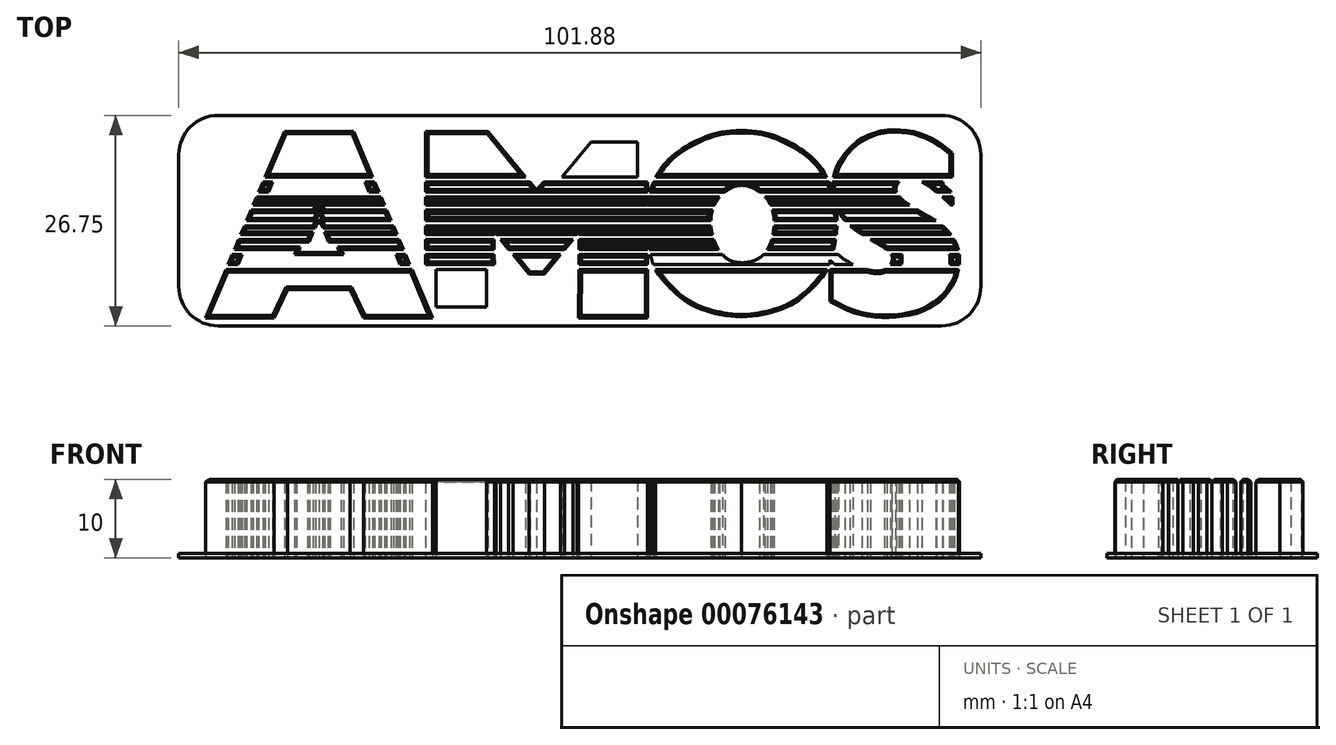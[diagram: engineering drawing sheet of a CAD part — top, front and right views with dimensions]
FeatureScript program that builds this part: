
annotation { "Feature Type Name" : "Feature", "Feature Type Description" : "" }
export const myFeature = defineFeature(function(context is Context, id is Id, definition is map)
    precondition{}
    {
        {
            var Q0;
            Q0=qCreatedBy(makeId("Top.planeOp"),FACE);
            var sketch = newSketch(context, id + "F0", { "sketchPlane" : qUnion([Q0])});
            skLineSegment(sketch, "E0", {"start": v(-45.6, -34.47) * mm, "end": v(-36.87, -34.47) * mm});
            skLineSegment(sketch, "E1", {"start": v(-36.87, -34.47) * mm, "end": v(-35.18, -30.82) * mm});
            skLineSegment(sketch, "E2", {"start": v(-35.18, -30.82) * mm, "end": v(-31.2, -30.82) * mm});
            skLineSegment(sketch, "E3", {"start": v(-45.6, -34.47) * mm, "end": v(-35.6, -10.76) * mm});
            skLineSegment(sketch, "E4", {"start": v(-35.6, -10.76) * mm, "end": v(-31.2, -10.76) * mm});
            skLineSegment(sketch, "E5", {"start": v(-31.2, -10.76) * mm, "end": v(-31.2, -30.82) * mm});
            skLineSegment(sketch, "E6", {"start": v(-43.85, -33.24) * mm, "end": v(-34.99, -12.25) * mm});
            skLineSegment(sketch, "E7", {"start": v(-34.99, -12.25) * mm, "end": v(-31.2, -12.25) * mm});
            skLineSegment(sketch, "E8", {"start": v(-43.85, -33.24) * mm, "end": v(-37.5, -33.24) * mm});
            skLineSegment(sketch, "E9", {"start": v(-37.5, -33.24) * mm, "end": v(-35.93, -29.53) * mm});
            skLineSegment(sketch, "E10", {"start": v(-35.93, -29.53) * mm, "end": v(-31.2, -29.53) * mm});
            skLineSegment(sketch, "E11", {"start": v(-31.2, -26.43) * mm, "end": v(-34.3, -26.43) * mm});
            skLineSegment(sketch, "E12", {"start": v(-34.3, -26.43) * mm, "end": v(-31.2, -19.09) * mm});
            skLineSegment(sketch, "E13", {"start": v(-31.2, -16.54) * mm, "end": v(-36.8, -16.54) * mm});
            skLineSegment(sketch, "E14", {"start": v(-36.8, -16.54) * mm, "end": v(-37.07, -17.19) * mm});
            skLineSegment(sketch, "E15", {"start": v(-37.07, -17.19) * mm, "end": v(-31.2, -17.19) * mm});
            skLineSegment(sketch, "E16", {"start": v(-31.2, -18.44) * mm, "end": v(-37.6, -18.44) * mm});
            skLineSegment(sketch, "E17", {"start": v(-37.6, -18.44) * mm, "end": v(-37.88, -19.09) * mm});
            skLineSegment(sketch, "E18", {"start": v(-37.88, -19.09) * mm, "end": v(-31.2, -19.09) * mm});
            skLineSegment(sketch, "E19", {"start": v(-31.65, -20.13) * mm, "end": v(-38.32, -20.13) * mm});
            skLineSegment(sketch, "E20", {"start": v(-38.32, -20.13) * mm, "end": v(-38.59, -20.78) * mm});
            skLineSegment(sketch, "E21", {"start": v(-38.59, -20.78) * mm, "end": v(-31.92, -20.78) * mm});
            skLineSegment(sketch, "E22", {"start": v(-33.22, -23.86) * mm, "end": v(-39.9, -23.86) * mm});
            skLineSegment(sketch, "E23", {"start": v(-39.9, -23.86) * mm, "end": v(-40.16, -24.5) * mm});
            skLineSegment(sketch, "E24", {"start": v(-40.16, -24.5) * mm, "end": v(-33.5, -24.5) * mm});
            skLineSegment(sketch, "E25", {"start": v(-34.03, -25.78) * mm, "end": v(-40.7, -25.78) * mm});
            skLineSegment(sketch, "E26", {"start": v(-40.7, -25.78) * mm, "end": v(-40.98, -26.43) * mm});
            skLineSegment(sketch, "E27", {"start": v(-40.98, -26.43) * mm, "end": v(-34.3, -26.43) * mm});
            skLineSegment(sketch, "E28", {"start": v(-31.2, -27.66) * mm, "end": v(-41.5, -27.66) * mm});
            skLineSegment(sketch, "E29", {"start": v(-41.5, -27.66) * mm, "end": v(-41.78, -28.33) * mm});
            skLineSegment(sketch, "E30", {"start": v(-41.78, -28.33) * mm, "end": v(-31.2, -28.33) * mm});
            skLineSegment(sketch, "E31", {"start": v(-32.48, -22.11) * mm, "end": v(-39.15, -22.11) * mm});
            skLineSegment(sketch, "E32", {"start": v(-32.76, -22.76) * mm, "end": v(-39.43, -22.76) * mm});
            skLineSegment(sketch, "E33", {"start": v(-31.2, -21.08) * mm, "end": v(-33.1, -25.55) * mm});
            skLineSegment(sketch, "E34", {"start": v(-33.1, -25.55) * mm, "end": v(-31.2, -25.55) * mm});
            skLineSegment(sketch, "E35.MirrorCS", {"start": v(-25.6, -16.54) * mm, "end": v(-25.34, -17.19) * mm});
            skLineSegment(sketch, "E36.MirrorCS", {"start": v(-22.52, -23.86) * mm, "end": v(-22.24, -24.5) * mm});
            skLineSegment(sketch, "E37.MirrorCS", {"start": v(-20.91, -27.66) * mm, "end": v(-20.63, -28.33) * mm});
            skLineSegment(sketch, "E38.MirrorCS", {"start": v(-21.7, -25.78) * mm, "end": v(-21.43, -26.43) * mm});
            skLineSegment(sketch, "E39.MirrorCS", {"start": v(-24.8, -18.44) * mm, "end": v(-24.53, -19.09) * mm});
            skLineSegment(sketch, "E40.MirrorCS", {"start": v(-24.1, -20.13) * mm, "end": v(-23.82, -20.78) * mm});
            skLineSegment(sketch, "E41.MirrorCS", {"start": v(-20.63, -28.33) * mm, "end": v(-31.2, -28.33) * mm});
            skLineSegment(sketch, "E42.MirrorCS", {"start": v(-31.2, -27.66) * mm, "end": v(-20.91, -27.66) * mm});
            skLineSegment(sketch, "E43.MirrorCS", {"start": v(-21.43, -26.43) * mm, "end": v(-28.1, -26.43) * mm});
            skLineSegment(sketch, "E44.MirrorCS", {"start": v(-29.19, -23.86) * mm, "end": v(-22.52, -23.86) * mm});
            skLineSegment(sketch, "E45.MirrorCS", {"start": v(-28.1, -26.43) * mm, "end": v(-31.2, -19.09) * mm});
            skLineSegment(sketch, "E46.MirrorCS", {"start": v(-29.65, -22.76) * mm, "end": v(-22.98, -22.76) * mm});
            skLineSegment(sketch, "E47.MirrorCS", {"start": v(-28.38, -25.78) * mm, "end": v(-21.7, -25.78) * mm});
            skLineSegment(sketch, "E48.MirrorCS", {"start": v(-31.2, -18.44) * mm, "end": v(-24.8, -18.44) * mm});
            skLineSegment(sketch, "E49.MirrorCS", {"start": v(-30.76, -20.13) * mm, "end": v(-24.1, -20.13) * mm});
            skLineSegment(sketch, "E50.MirrorCS", {"start": v(-26.47, -29.53) * mm, "end": v(-31.2, -29.53) * mm});
            skLineSegment(sketch, "E51.MirrorCS", {"start": v(-18.55, -33.24) * mm, "end": v(-24.9, -33.24) * mm});
            skLineSegment(sketch, "E52.MirrorCS", {"start": v(-27.42, -12.25) * mm, "end": v(-31.2, -12.25) * mm});
            skLineSegment(sketch, "E53.MirrorCS", {"start": v(-18.55, -33.24) * mm, "end": v(-27.42, -12.25) * mm});
            skLineSegment(sketch, "E54.MirrorCS", {"start": v(-26.82, -10.76) * mm, "end": v(-31.2, -10.76) * mm});
            skLineSegment(sketch, "E55.MirrorCS", {"start": v(-25.34, -17.19) * mm, "end": v(-31.2, -17.19) * mm});
            skLineSegment(sketch, "E56.MirrorCS", {"start": v(-16.8, -34.47) * mm, "end": v(-26.82, -10.76) * mm});
            skLineSegment(sketch, "E57.MirrorCS", {"start": v(-27.23, -30.82) * mm, "end": v(-31.2, -30.82) * mm});
            skLineSegment(sketch, "E58.MirrorCS", {"start": v(-24.9, -33.24) * mm, "end": v(-26.47, -29.53) * mm});
            skLineSegment(sketch, "E59.MirrorCS", {"start": v(-25.54, -34.47) * mm, "end": v(-27.23, -30.82) * mm});
            skLineSegment(sketch, "E60.MirrorCS", {"start": v(-29.93, -22.11) * mm, "end": v(-23.26, -22.11) * mm});
            skLineSegment(sketch, "E61.MirrorCS", {"start": v(-29.32, -25.55) * mm, "end": v(-31.2, -25.55) * mm});
            skLineSegment(sketch, "E62.MirrorCS", {"start": v(-16.8, -34.47) * mm, "end": v(-25.54, -34.47) * mm});
            skLineSegment(sketch, "E63.MirrorCS", {"start": v(-23.82, -20.78) * mm, "end": v(-30.5, -20.78) * mm});
            skLineSegment(sketch, "E64.MirrorCS", {"start": v(-24.53, -19.09) * mm, "end": v(-31.2, -19.09) * mm});
            skLineSegment(sketch, "E65.MirrorCS", {"start": v(-31.2, -16.54) * mm, "end": v(-25.6, -16.54) * mm});
            skLineSegment(sketch, "E66.MirrorCS", {"start": v(-31.2, -21.08) * mm, "end": v(-29.32, -25.55) * mm});
            skLineSegment(sketch, "E67.MirrorCS", {"start": v(-31.2, -26.43) * mm, "end": v(-28.1, -26.43) * mm});
            skLineSegment(sketch, "E68.MirrorCS", {"start": v(-22.24, -24.5) * mm, "end": v(-28.91, -24.5) * mm});
            skLineSegment(sketch, "E69", {"start": v(-8.88, -34.47) * mm, "end": v(-17.64, -34.47) * mm});
            skLineSegment(sketch, "E70", {"start": v(-17.64, -34.47) * mm, "end": v(-17.64, -10.76) * mm});
            skLineSegment(sketch, "E71", {"start": v(-17.64, -10.76) * mm, "end": v(-9.73, -10.76) * mm});
            skLineSegment(sketch, "E72", {"start": v(-9.73, -10.76) * mm, "end": v(-3.54, -18.24) * mm});
            skLineSegment(sketch, "E73", {"start": v(-3.54, -28.9) * mm, "end": v(-4.5, -28.9) * mm});
            skLineSegment(sketch, "E74", {"start": v(-4.5, -28.9) * mm, "end": v(-8.95, -23.54) * mm});
            skLineSegment(sketch, "E75", {"start": v(-8.95, -23.54) * mm, "end": v(-8.88, -34.47) * mm});
            skLineSegment(sketch, "E76", {"start": v(-3.54, -28.9) * mm, "end": v(-3.54, -18.24) * mm});
            skLineSegment(sketch, "E77", {"start": v(-16.34, -12.09) * mm, "end": v(-10.43, -12.09) * mm});
            skLineSegment(sketch, "E78", {"start": v(-10.43, -12.09) * mm, "end": v(-3.54, -20.42) * mm});
            skLineSegment(sketch, "E79", {"start": v(-16.34, -12.09) * mm, "end": v(-16.34, -33.1) * mm});
            skLineSegment(sketch, "E80", {"start": v(-16.34, -33.1) * mm, "end": v(-9.91, -33.1) * mm});
            skLineSegment(sketch, "E81", {"start": v(-9.91, -33.1) * mm, "end": v(-9.99, -20.8) * mm});
            skLineSegment(sketch, "E82", {"start": v(-9.99, -20.8) * mm, "end": v(-4.44, -27.52) * mm});
            skLineSegment(sketch, "E83", {"start": v(-4.44, -27.52) * mm, "end": v(-3.54, -27.52) * mm});
            skLineSegment(sketch, "E84", {"start": v(-36.8, -16.54) * mm, "end": v(52.85, -16.54) * mm});
            skLineSegment(sketch, "E85", {"start": v(-37.07, -17.19) * mm, "end": v(52.85, -17.19) * mm});
            skLineSegment(sketch, "E86", {"start": v(-37.6, -18.44) * mm, "end": v(52.85, -18.44) * mm});
            skLineSegment(sketch, "E87", {"start": v(-37.88, -19.09) * mm, "end": v(52.85, -19.09) * mm});
            skLineSegment(sketch, "E88", {"start": v(-38.32, -20.13) * mm, "end": v(52.85, -20.13) * mm});
            skLineSegment(sketch, "E89", {"start": v(-38.59, -20.78) * mm, "end": v(52.85, -20.78) * mm});
            skLineSegment(sketch, "E90", {"start": v(-39.15, -22.11) * mm, "end": v(52.85, -22.11) * mm});
            skLineSegment(sketch, "E91", {"start": v(-39.43, -22.76) * mm, "end": v(52.85, -22.76) * mm});
            skLineSegment(sketch, "E92", {"start": v(-39.9, -23.86) * mm, "end": v(52.85, -23.86) * mm});
            skLineSegment(sketch, "E93", {"start": v(-40.16, -24.5) * mm, "end": v(52.85, -24.5) * mm});
            skLineSegment(sketch, "E94", {"start": v(-40.7, -25.78) * mm, "end": v(52.85, -25.78) * mm});
            skLineSegment(sketch, "E95", {"start": v(-40.98, -26.43) * mm, "end": v(52.85, -26.43) * mm});
            skLineSegment(sketch, "E96", {"start": v(-41.5, -27.66) * mm, "end": v(52.85, -27.66) * mm});
            skLineSegment(sketch, "E97", {"start": v(-41.78, -28.33) * mm, "end": v(52.85, -28.33) * mm});
            skLineSegment(sketch, "E98.MirrorCS", {"start": v(-3.54, -28.9) * mm, "end": v(-2.57, -28.9) * mm});
            skLineSegment(sketch, "E99.MirrorCS", {"start": v(-2.65, -27.52) * mm, "end": v(-3.54, -27.52) * mm});
            skLineSegment(sketch, "E100.MirrorCS", {"start": v(1.87, -23.54) * mm, "end": v(1.8, -34.47) * mm});
            skLineSegment(sketch, "E101.MirrorCS", {"start": v(3.35, -12.09) * mm, "end": v(-3.54, -20.42) * mm});
            skLineSegment(sketch, "E102.MirrorCS", {"start": v(-2.57, -28.9) * mm, "end": v(1.87, -23.54) * mm});
            skLineSegment(sketch, "E103.MirrorCS", {"start": v(2.65, -10.76) * mm, "end": v(-3.54, -18.24) * mm});
            skLineSegment(sketch, "E104.MirrorCS", {"start": v(10.56, -10.76) * mm, "end": v(2.65, -10.76) * mm});
            skLineSegment(sketch, "E105.MirrorCS", {"start": v(2.9, -20.8) * mm, "end": v(-2.65, -27.52) * mm});
            skLineSegment(sketch, "E106.MirrorCS", {"start": v(10.56, -34.47) * mm, "end": v(10.56, -10.76) * mm});
            skLineSegment(sketch, "E107.MirrorCS", {"start": v(2.83, -33.1) * mm, "end": v(2.9, -20.8) * mm});
            skLineSegment(sketch, "E108.MirrorCS", {"start": v(1.8, -34.47) * mm, "end": v(10.56, -34.47) * mm});
            skLineSegment(sketch, "E109.MirrorCS", {"start": v(9.26, -33.1) * mm, "end": v(2.83, -33.1) * mm});
            skLineSegment(sketch, "E110.MirrorCS", {"start": v(9.26, -12.09) * mm, "end": v(3.35, -12.09) * mm});
            skLineSegment(sketch, "E111.MirrorCS", {"start": v(9.26, -12.09) * mm, "end": v(9.26, -33.1) * mm});
            skFitSpline(sketch, "E112", {"points": [v(22.46, -10.68) * mm, v(18.17, -11.35) * mm, v(14.47, -13.3) * mm, v(11.9, -16.04) * mm, v(10.3, -21.26) * mm, v(11.13, -27.27) * mm, v(12.26, -29.34) * mm, v(15.78, -32.6) * mm, v(22.46, -34.35) * mm], "startDerivative": vector(-46.81, 1.11) * mm, "endDerivative": vector(48.92, -2.68) * mm});
            skLineSegment(sketch, "E113", {"start": v(22.46, -10.68) * mm, "end": v(22.46, -34.35) * mm});
            skFitSpline(sketch, "E114.0", {"points": [v(22.43, -11.92) * mm, v(21.97, -11.9) * mm, v(21.17, -11.92) * mm, v(20.2, -12.04) * mm, v(19.5, -12.21) * mm, v(18.94, -12.4) * mm, v(18.5, -12.56) * mm, v(18.03, -12.74) * mm, v(17.4, -13.02) * mm, v(16.63, -13.4) * mm, v(15.73, -13.93) * mm, v(14.92, -14.48) * mm, v(14.24, -15.07) * mm, v(13.64, -15.7) * mm, v(13.1, -16.44) * mm, v(12.6, -17.3) * mm, v(12.17, -18.3) * mm, v(11.83, -19.38) * mm, v(11.6, -20.56) * mm, v(11.5, -21.8) * mm, v(11.57, -23.15) * mm, v(11.73, -24.49) * mm, v(11.94, -25.52) * mm, v(12.12, -26.24) * mm, v(12.26, -26.72) * mm, v(12.4, -27.12) * mm, v(12.57, -27.55) * mm, v(12.75, -27.89) * mm, v(12.99, -28.24) * mm, v(13.21, -28.54) * mm, v(13.49, -28.9) * mm, v(13.9, -29.38) * mm, v(14.5, -30.03) * mm, v(15.35, -30.8) * mm, v(16.13, -31.36) * mm, v(16.8, -31.75) * mm, v(17.51, -32.1) * mm, v(18.48, -32.45) * mm, v(20.16, -32.89) * mm, v(21.56, -33.05) * mm, v(22.53, -33.1) * mm]});
            skFitSpline(sketch, "E115.MirrorCS", {"points": [v(22.46, -10.68) * mm, v(26.75, -11.35) * mm, v(30.45, -13.3) * mm, v(33.02, -16.04) * mm, v(34.6, -21.26) * mm, v(33.78, -27.27) * mm, v(32.65, -29.34) * mm, v(29.14, -32.6) * mm, v(22.46, -34.35) * mm], "startDerivative": vector(46.81, 1.11) * mm, "endDerivative": vector(-48.92, -2.68) * mm});
            skFitSpline(sketch, "E116.0", {"points": [v(22.49, -11.97) * mm, v(22.94, -11.96) * mm, v(23.74, -11.98) * mm, v(24.7, -12.1) * mm, v(25.4, -12.26) * mm, v(25.96, -12.44) * mm, v(26.4, -12.6) * mm, v(26.86, -12.8) * mm, v(27.49, -13.06) * mm, v(28.27, -13.45) * mm, v(29.16, -13.97) * mm, v(29.96, -14.53) * mm, v(30.64, -15.1) * mm, v(31.24, -15.74) * mm, v(31.77, -16.47) * mm, v(32.27, -17.33) * mm, v(32.7, -18.3) * mm, v(33.04, -19.4) * mm, v(33.27, -20.56) * mm, v(33.35, -21.8) * mm, v(33.3, -23.15) * mm, v(33.13, -24.48) * mm, v(32.93, -25.5) * mm, v(32.75, -26.23) * mm, v(32.6, -26.7) * mm, v(32.47, -27.1) * mm, v(32.3, -27.53) * mm, v(32.12, -27.86) * mm, v(31.89, -28.21) * mm, v(31.66, -28.51) * mm, v(31.4, -28.86) * mm, v(30.98, -29.35) * mm, v(30.38, -30) * mm, v(29.53, -30.76) * mm, v(28.75, -31.32) * mm, v(28.1, -31.7) * mm, v(27.38, -32.05) * mm, v(26.42, -32.4) * mm, v(24.75, -32.84) * mm, v(23.35, -33) * mm, v(22.39, -33.06) * mm]});
            skFitSpline(sketch, "E117", {"points": [v(49.24, -13.5) * mm, v(46.32, -11.49) * mm, v(42.17, -10.55) * mm, v(38.34, -11.36) * mm, v(35.36, -13.9) * mm, v(34.1, -16.89) * mm, v(34.19, -19.42) * mm, v(34.98, -21.26) * mm, v(36.8, -23.19) * mm, v(40.2, -25.3) * mm, v(41.55, -26.49) * mm, v(41.5, -27.5) * mm, v(40.5, -28.4) * mm, v(38.54, -28.35) * mm, v(35.81, -27.2) * mm, v(33.68, -25.44) * mm], "startDerivative": vector(-34.4, 29.23) * mm, "endDerivative": vector(-30.32, 27.7) * mm});
            skFitSpline(sketch, "E118", {"points": [v(33.68, -32.37) * mm, v(37.2, -33.94) * mm, v(41.36, -34.37) * mm, v(45.32, -33.65) * mm, v(48.33, -31.65) * mm, v(49.9, -28.93) * mm, v(50.1, -26.19) * mm, v(49.33, -24.24) * mm, v(47.6, -22.42) * mm, v(44.8, -20.76) * mm, v(42.36, -18.85) * mm, v(42.12, -17.85) * mm, v(42.74, -17) * mm, v(44.32, -16.74) * mm, v(47.14, -18.37) * mm, v(49.34, -20.42) * mm], "startDerivative": vector(43.54, -22.9) * mm, "endDerivative": vector(27.49, -30.17) * mm});
            skLineSegment(sketch, "E119", {"start": v(33.68, -25.44) * mm, "end": v(33.68, -32.37) * mm});
            skLineSegment(sketch, "E120", {"start": v(49.24, -13.5) * mm, "end": v(49.34, -20.42) * mm});
            skFitSpline(sketch, "E121.0", {"points": [v(48.45, -14.43) * mm, v(48.1, -14.13) * mm, v(47.4, -13.56) * mm, v(46.51, -12.95) * mm, v(45.75, -12.56) * mm, v(45.12, -12.3) * mm, v(44.45, -12.1) * mm, v(43.51, -11.88) * mm, v(42.3, -11.75) * mm, v(40.95, -11.8) * mm, v(39.69, -12.09) * mm, v(38.53, -12.6) * mm, v(37.44, -13.38) * mm, v(36.52, -14.33) * mm, v(35.84, -15.36) * mm, v(35.48, -16.26) * mm, v(35.31, -16.97) * mm, v(35.22, -17.66) * mm, v(35.24, -18.35) * mm, v(35.34, -18.98) * mm, v(35.49, -19.57) * mm, v(35.7, -20.08) * mm, v(36, -20.59) * mm, v(36.35, -21.1) * mm, v(36.8, -21.6) * mm, v(37.32, -22.04) * mm, v(37.66, -22.3) * mm, v(38.03, -22.56) * mm, v(38.55, -22.9) * mm, v(39.23, -23.3) * mm, v(39.9, -23.7) * mm, v(40.57, -24.08) * mm, v(41.18, -24.45) * mm, v(41.65, -24.78) * mm, v(42.01, -25.09) * mm, v(42.26, -25.35) * mm, v(42.46, -25.6) * mm, v(42.6, -25.84) * mm, v(42.72, -26.1) * mm, v(42.83, -26.44) * mm, v(42.89, -27) * mm, v(42.79, -27.65) * mm, v(42.46, -28.34) * mm, v(42.07, -28.82) * mm, v(41.68, -29.15) * mm, v(41.35, -29.36) * mm, v(40.98, -29.54) * mm, v(40.46, -29.7) * mm, v(39.82, -29.77) * mm, v(39.09, -29.72) * mm, v(38.5, -29.6) * mm, v(38.04, -29.5) * mm, v(37.58, -29.36) * mm, v(36.99, -29.16) * mm, v(36.28, -28.86) * mm, v(35.6, -28.52) * mm, v(34.94, -28.1) * mm, v(34.35, -27.67) * mm, v(33.63, -27.07) * mm, v(33.16, -26.62) * mm, v(32.86, -26.34) * mm]});
            skLineSegment(sketch, "E121.1", {"start": v(48.02, -14.07) * mm, "end": v(48.07, -17.55) * mm});
            skFitSpline(sketch, "E121.2", {"points": [v(34.25, -31.28) * mm, v(34.71, -31.52) * mm, v(35.6, -32) * mm, v(36.65, -32.47) * mm, v(37.5, -32.76) * mm, v(38.15, -32.92) * mm, v(38.84, -33.04) * mm, v(39.56, -33.12) * mm, v(40.3, -33.16) * mm, v(41.05, -33.16) * mm, v(41.8, -33.13) * mm, v(42.78, -33.04) * mm, v(43.7, -32.88) * mm, v(44.56, -32.64) * mm, v(45.37, -32.33) * mm, v(46.31, -31.8) * mm, v(47.29, -31.02) * mm, v(48.04, -30.11) * mm, v(48.5, -29.28) * mm, v(48.74, -28.6) * mm, v(48.9, -27.88) * mm, v(48.97, -27.16) * mm, v(48.92, -26.5) * mm, v(48.84, -26.08) * mm, v(48.72, -25.69) * mm, v(48.55, -25.31) * mm, v(48.33, -24.93) * mm, v(48.04, -24.54) * mm, v(47.72, -24.15) * mm, v(47.34, -23.78) * mm, v(47, -23.5) * mm, v(46.7, -23.29) * mm, v(46.23, -22.97) * mm, v(45.57, -22.6) * mm, v(44.71, -22.13) * mm, v(44.03, -21.73) * mm, v(43.33, -21.3) * mm, v(42.66, -20.83) * mm, v(42.04, -20.32) * mm, v(41.5, -19.78) * mm, v(41.13, -19.23) * mm, v(40.94, -18.72) * mm, v(40.86, -18.31) * mm, v(40.86, -17.9) * mm, v(40.93, -17.52) * mm, v(41.05, -17.16) * mm, v(41.28, -16.72) * mm, v(41.68, -16.24) * mm, v(42.3, -15.8) * mm, v(43.04, -15.52) * mm, v(43.71, -15.44) * mm, v(44.27, -15.48) * mm, v(44.7, -15.57) * mm, v(45.1, -15.7) * mm, v(45.62, -15.9) * mm, v(46.24, -16.22) * mm, v(46.93, -16.67) * mm, v(47.59, -17.16) * mm, v(48.2, -17.64) * mm, v(48.75, -18.12) * mm, v(49.46, -18.77) * mm, v(49.94, -19.26) * mm, v(50.24, -19.6) * mm]});
            skLineSegment(sketch, "E121.3", {"start": v(34.9, -28.08) * mm, "end": v(34.9, -31.62) * mm});
            skLineSegment(sketch, "E122", {"start": v(-36.8, -16.54) * mm, "end": v(-52.11, -16.54) * mm});
            skLineSegment(sketch, "E123", {"start": v(-37.07, -17.19) * mm, "end": v(-52.11, -17.19) * mm});
            skLineSegment(sketch, "E124", {"start": v(-37.6, -18.44) * mm, "end": v(-52.11, -18.44) * mm});
            skLineSegment(sketch, "E125", {"start": v(-37.88, -19.09) * mm, "end": v(-52.11, -19.09) * mm});
            skLineSegment(sketch, "E126", {"start": v(-38.32, -20.13) * mm, "end": v(-52.11, -20.13) * mm});
            skLineSegment(sketch, "E127", {"start": v(-38.59, -20.78) * mm, "end": v(-52.11, -20.78) * mm});
            skLineSegment(sketch, "E128", {"start": v(-39.15, -22.11) * mm, "end": v(-52.11, -22.11) * mm});
            skLineSegment(sketch, "E129", {"start": v(-39.43, -22.76) * mm, "end": v(-52.11, -22.76) * mm});
            skLineSegment(sketch, "E130", {"start": v(-39.9, -23.86) * mm, "end": v(-52.11, -23.86) * mm});
            skLineSegment(sketch, "E131", {"start": v(-40.16, -24.5) * mm, "end": v(-52.11, -24.5) * mm});
            skLineSegment(sketch, "E132", {"start": v(-40.7, -25.78) * mm, "end": v(-52.11, -25.78) * mm});
            skLineSegment(sketch, "E133", {"start": v(-40.98, -26.43) * mm, "end": v(-52.11, -26.43) * mm});
            skLineSegment(sketch, "E134", {"start": v(-41.5, -27.66) * mm, "end": v(-52.11, -27.66) * mm});
            skLineSegment(sketch, "E135", {"start": v(-41.78, -28.33) * mm, "end": v(-52.11, -28.33) * mm});
            skFitSpline(sketch, "E136", {"points": [v(22.46, -17.61) * mm, v(19.7, -19.09) * mm, v(18.57, -22.4) * mm, v(20.05, -26.43) * mm, v(22.46, -27.46) * mm, v(25.25, -26.43) * mm, v(26.62, -22.4) * mm, v(25.48, -19.09) * mm, v(22.46, -17.61) * mm]});
            skLineSegment(sketch, "E137.bottom", {"start": v(-47.15, -8.85) * mm, "end": v(52.85, -8.85) * mm});
            skLineSegment(sketch, "E137.top", {"start": v(-47.15, -35.44) * mm, "end": v(52.85, -35.44) * mm});
            skLineSegment(sketch, "E137.left", {"start": v(-47.15, -8.85) * mm, "end": v(-47.15, -35.44) * mm});
            skLineSegment(sketch, "E137.right", {"start": v(52.85, -8.85) * mm, "end": v(52.85, -35.44) * mm, "construction": true});
            skSolve(sketch);
        }
        {
            var Q0;
            {var subQ5=sQuery(id+"F0.wireOp",EDGE,"E4");Q0=makeQuery(id+"F0.imprint","IMPRINT",FACE,{"disambiguationData":[TD([[makeQuery(id+"F0.imprint","IMPRINT",EDGE,{"derivedFrom":subQ5}),-1.0]])]});}
            extrude(context, id + "F1", {"entities" : qUnion([Q0]), "depth" : 10 * mm});
        }
        {
            var Q0;
            {var subQ2=sQuery(id+"F0.wireOp",EDGE,"E52.MirrorCS");Q0=makeQuery(id+"F0.imprint","IMPRINT",FACE,{"disambiguationData":[TD([[makeQuery(id+"F0.imprint","IMPRINT",EDGE,{"derivedFrom":subQ2}),-1.0]])]});}
            var Q1;
            {var subQ0=sQuery(id+"F0.wireOp",EDGE,"E52.MirrorCS");Q1=makeQuery(id+"F0.imprint","IMPRINT",FACE,{"disambiguationData":[TD([[makeQuery(id+"F0.imprint","IMPRINT",EDGE,{"derivedFrom":subQ0}),1.0]])]});}
            var Q2;
            {var subQ0=sQuery(id+"F0.wireOp",EDGE,"E7");Q2=makeQuery(id+"F0.imprint","IMPRINT",FACE,{"disambiguationData":[TD([[makeQuery(id+"F0.imprint","IMPRINT",EDGE,{"derivedFrom":subQ0}),-1.0]])]});}
            var Q3;
            {var subQ0=sQuery(id+"F0.wireOp",EDGE,"E86");var subQ1=sQuery(id+"F0.wireOp",EDGE,"E53.MirrorCS");var subQ2=makeQuery(id+"F0.imprint","INTERSECT",VERTEX,{"derivedFrom":[subQ1,subQ0]});Q3=makeQuery(id+"F0.imprint","IMPRINT",FACE,{"disambiguationData":[TD([[makeQuery(id+"F0.imprint","IMPRINT",EDGE,{"disambiguationData":[TD([[subQ2,-1.0]])],"derivedFrom":subQ1}),-1.0]])]});}
            var Q4;
            {var subQ0=sQuery(id+"F0.wireOp",EDGE,"E88");var subQ1=sQuery(id+"F0.wireOp",EDGE,"E53.MirrorCS");var subQ2=makeQuery(id+"F0.imprint","INTERSECT",VERTEX,{"derivedFrom":[subQ1,subQ0]});Q4=makeQuery(id+"F0.imprint","IMPRINT",FACE,{"disambiguationData":[TD([[makeQuery(id+"F0.imprint","IMPRINT",EDGE,{"disambiguationData":[TD([[subQ2,-1.0]])],"derivedFrom":subQ1}),-1.0]])]});}
            var Q5;
            {var subQ0=sQuery(id+"F0.wireOp",EDGE,"E90");var subQ1=sQuery(id+"F0.wireOp",EDGE,"E53.MirrorCS");var subQ2=makeQuery(id+"F0.imprint","INTERSECT",VERTEX,{"derivedFrom":[subQ1,subQ0]});Q5=makeQuery(id+"F0.imprint","IMPRINT",FACE,{"disambiguationData":[TD([[makeQuery(id+"F0.imprint","IMPRINT",EDGE,{"disambiguationData":[TD([[subQ2,-1.0]])],"derivedFrom":subQ1}),-1.0]])]});}
            var Q6;
            {var subQ0=sQuery(id+"F0.wireOp",EDGE,"E92");var subQ1=sQuery(id+"F0.wireOp",EDGE,"E53.MirrorCS");var subQ2=makeQuery(id+"F0.imprint","INTERSECT",VERTEX,{"derivedFrom":[subQ1,subQ0]});Q6=makeQuery(id+"F0.imprint","IMPRINT",FACE,{"disambiguationData":[TD([[makeQuery(id+"F0.imprint","IMPRINT",EDGE,{"disambiguationData":[TD([[subQ2,-1.0]])],"derivedFrom":subQ1}),-1.0]])]});}
            var Q7;
            {var subQ0=sQuery(id+"F0.wireOp",EDGE,"E94");var subQ1=sQuery(id+"F0.wireOp",EDGE,"E53.MirrorCS");var subQ2=makeQuery(id+"F0.imprint","INTERSECT",VERTEX,{"derivedFrom":[subQ1,subQ0]});Q7=makeQuery(id+"F0.imprint","IMPRINT",FACE,{"disambiguationData":[TD([[makeQuery(id+"F0.imprint","IMPRINT",EDGE,{"disambiguationData":[TD([[subQ2,-1.0]])],"derivedFrom":subQ1}),-1.0]])]});}
            var Q8;
            {var subQ0=sQuery(id+"F0.wireOp",EDGE,"E96");var subQ1=sQuery(id+"F0.wireOp",EDGE,"E53.MirrorCS");var subQ2=makeQuery(id+"F0.imprint","INTERSECT",VERTEX,{"derivedFrom":[subQ1,subQ0]});Q8=makeQuery(id+"F0.imprint","IMPRINT",FACE,{"disambiguationData":[TD([[makeQuery(id+"F0.imprint","IMPRINT",EDGE,{"disambiguationData":[TD([[subQ2,-1.0]])],"derivedFrom":subQ1}),-1.0]])]});}
            var Q9;
            {var subQ11=sQuery(id+"F0.wireOp",EDGE,"E50.MirrorCS");Q9=makeQuery(id+"F0.imprint","IMPRINT",FACE,{"disambiguationData":[TD([[makeQuery(id+"F0.imprint","IMPRINT",EDGE,{"derivedFrom":subQ11}),1.0]])]});}
            var Q10;
            {var subQ0=sQuery(id+"F0.wireOp",EDGE,"E69");var subQ1=sQuery(id+"F0.wireOp",EDGE,"E56.MirrorCS");var subQ2=makeQuery(id+"F0.imprint","INTERSECT",VERTEX,{"derivedFrom":[subQ1,subQ0]});Q10=makeQuery(id+"F0.imprint","IMPRINT",FACE,{"disambiguationData":[TD([[makeQuery(id+"F0.imprint","IMPRINT",EDGE,{"disambiguationData":[TD([[subQ2,-1.0]])],"derivedFrom":subQ1}),1.0]])]});}
            var Q11;
            {var subQ1=sQuery(id+"F0.wireOp",EDGE,"E0");Q11=makeQuery(id+"F0.imprint","IMPRINT",FACE,{"disambiguationData":[TD([[makeQuery(id+"F0.imprint","IMPRINT",EDGE,{"derivedFrom":subQ1}),1.0]])]});}
            var Q12;
            {var subQ0=sQuery(id+"F0.wireOp",EDGE,"E134");var subQ1=sQuery(id+"F0.wireOp",EDGE,"E3");var subQ2=makeQuery(id+"F0.imprint","INTERSECT",VERTEX,{"derivedFrom":[subQ1,subQ0]});Q12=makeQuery(id+"F0.imprint","IMPRINT",FACE,{"disambiguationData":[TD([[makeQuery(id+"F0.imprint","IMPRINT",EDGE,{"disambiguationData":[TD([[subQ2,-1.0]])],"derivedFrom":subQ1}),-1.0]])]});}
            var Q13;
            {var subQ0=sQuery(id+"F0.wireOp",EDGE,"E132");var subQ1=sQuery(id+"F0.wireOp",EDGE,"E3");var subQ2=makeQuery(id+"F0.imprint","INTERSECT",VERTEX,{"derivedFrom":[subQ1,subQ0]});Q13=makeQuery(id+"F0.imprint","IMPRINT",FACE,{"disambiguationData":[TD([[makeQuery(id+"F0.imprint","IMPRINT",EDGE,{"disambiguationData":[TD([[subQ2,-1.0]])],"derivedFrom":subQ1}),-1.0]])]});}
            var Q14;
            {var subQ0=sQuery(id+"F0.wireOp",EDGE,"E130");var subQ1=sQuery(id+"F0.wireOp",EDGE,"E3");var subQ2=makeQuery(id+"F0.imprint","INTERSECT",VERTEX,{"derivedFrom":[subQ1,subQ0]});Q14=makeQuery(id+"F0.imprint","IMPRINT",FACE,{"disambiguationData":[TD([[makeQuery(id+"F0.imprint","IMPRINT",EDGE,{"disambiguationData":[TD([[subQ2,-1.0]])],"derivedFrom":subQ1}),-1.0]])]});}
            var Q15;
            {var subQ0=sQuery(id+"F0.wireOp",EDGE,"E128");var subQ1=sQuery(id+"F0.wireOp",EDGE,"E3");var subQ2=makeQuery(id+"F0.imprint","INTERSECT",VERTEX,{"derivedFrom":[subQ1,subQ0]});Q15=makeQuery(id+"F0.imprint","IMPRINT",FACE,{"disambiguationData":[TD([[makeQuery(id+"F0.imprint","IMPRINT",EDGE,{"disambiguationData":[TD([[subQ2,-1.0]])],"derivedFrom":subQ1}),-1.0]])]});}
            var Q16;
            {var subQ0=sQuery(id+"F0.wireOp",EDGE,"E126");var subQ1=sQuery(id+"F0.wireOp",EDGE,"E3");var subQ2=makeQuery(id+"F0.imprint","INTERSECT",VERTEX,{"derivedFrom":[subQ1,subQ0]});Q16=makeQuery(id+"F0.imprint","IMPRINT",FACE,{"disambiguationData":[TD([[makeQuery(id+"F0.imprint","IMPRINT",EDGE,{"disambiguationData":[TD([[subQ2,-1.0]])],"derivedFrom":subQ1}),-1.0]])]});}
            var Q17;
            {var subQ0=sQuery(id+"F0.wireOp",EDGE,"E124");var subQ1=sQuery(id+"F0.wireOp",EDGE,"E3");var subQ2=makeQuery(id+"F0.imprint","INTERSECT",VERTEX,{"derivedFrom":[subQ1,subQ0]});Q17=makeQuery(id+"F0.imprint","IMPRINT",FACE,{"disambiguationData":[TD([[makeQuery(id+"F0.imprint","IMPRINT",EDGE,{"disambiguationData":[TD([[subQ2,-1.0]])],"derivedFrom":subQ1}),-1.0]])]});}
            var Q18;
            {var subQ0=sQuery(id+"F0.wireOp",EDGE,"E92");var subQ1=sQuery(id+"F0.wireOp",EDGE,"E12");var subQ2=makeQuery(id+"F0.imprint","INTERSECT",VERTEX,{"derivedFrom":[subQ1,subQ0]});Q18=makeQuery(id+"F0.imprint","IMPRINT",FACE,{"disambiguationData":[TD([[makeQuery(id+"F0.imprint","IMPRINT",EDGE,{"disambiguationData":[TD([[subQ2,-1.0]])],"derivedFrom":subQ1}),-1.0]])]});}
            var Q19;
            {var subQ5=sQuery(id+"F0.wireOp",EDGE,"E34");Q19=makeQuery(id+"F0.imprint","IMPRINT",FACE,{"disambiguationData":[TD([[makeQuery(id+"F0.imprint","IMPRINT",EDGE,{"derivedFrom":subQ5}),-1.0]])]});}
            var Q20;
            {var subQ1=sQuery(id+"F0.wireOp",EDGE,"E61.MirrorCS");Q20=makeQuery(id+"F0.imprint","IMPRINT",FACE,{"disambiguationData":[TD([[makeQuery(id+"F0.imprint","IMPRINT",EDGE,{"derivedFrom":subQ1}),1.0]])]});}
            var Q21;
            {var subQ0=sQuery(id+"F0.wireOp",EDGE,"E92");var subQ1=sQuery(id+"F0.wireOp",EDGE,"E45.MirrorCS");var subQ2=makeQuery(id+"F0.imprint","INTERSECT",VERTEX,{"derivedFrom":[subQ1,subQ0]});Q21=makeQuery(id+"F0.imprint","IMPRINT",FACE,{"disambiguationData":[TD([[makeQuery(id+"F0.imprint","IMPRINT",EDGE,{"disambiguationData":[TD([[subQ2,-1.0]])],"derivedFrom":subQ1}),1.0]])]});}
            var Q22;
            {var subQ3=sQuery(id+"F0.wireOp",EDGE,"E90");var subQ7=sQuery(id+"F0.wireOp",EDGE,"E45.MirrorCS");var subQ9=makeQuery(id+"F0.imprint","INTERSECT",VERTEX,{"derivedFrom":[subQ7,subQ3]});Q22=makeQuery(id+"F0.imprint","IMPRINT",FACE,{"disambiguationData":[TD([[makeQuery(id+"F0.imprint","IMPRINT",EDGE,{"disambiguationData":[TD([[subQ9,-1.0]])],"derivedFrom":subQ7}),1.0]])]});}
            var Q23;
            {var subQ3=sQuery(id+"F0.wireOp",EDGE,"E90");var subQ7=sQuery(id+"F0.wireOp",EDGE,"E12");var subQ9=makeQuery(id+"F0.imprint","INTERSECT",VERTEX,{"derivedFrom":[subQ7,subQ3]});Q23=makeQuery(id+"F0.imprint","IMPRINT",FACE,{"disambiguationData":[TD([[makeQuery(id+"F0.imprint","IMPRINT",EDGE,{"disambiguationData":[TD([[subQ9,-1.0]])],"derivedFrom":subQ7}),-1.0]])]});}
            var Q24;
            {var subQ1=sQuery(id+"F0.wireOp",EDGE,"E5");var subQ3=sQuery(id+"F0.wireOp",EDGE,"E88");var subQ4=makeQuery(id+"F0.imprint","INTERSECT",VERTEX,{"derivedFrom":[subQ1,subQ3]});Q24=makeQuery(id+"F0.imprint","IMPRINT",FACE,{"disambiguationData":[TD([[makeQuery(id+"F0.imprint","IMPRINT",EDGE,{"disambiguationData":[TD([[subQ4,-1.0]])],"derivedFrom":subQ3}),1.0]])]});}
            var Q25;
            {var subQ1=sQuery(id+"F0.wireOp",EDGE,"E5");var subQ3=sQuery(id+"F0.wireOp",EDGE,"E88");var subQ4=makeQuery(id+"F0.imprint","INTERSECT",VERTEX,{"derivedFrom":[subQ1,subQ3]});Q25=makeQuery(id+"F0.imprint","IMPRINT",FACE,{"disambiguationData":[TD([[makeQuery(id+"F0.imprint","IMPRINT",EDGE,{"disambiguationData":[TD([[subQ4,1.0]])],"derivedFrom":subQ3}),1.0]])]});}
            var Q26;
            {var subQ0=sQuery(id+"F0.wireOp",EDGE,"E50.MirrorCS");Q26=makeQuery(id+"F0.imprint","IMPRINT",FACE,{"disambiguationData":[TD([[makeQuery(id+"F0.imprint","IMPRINT",EDGE,{"derivedFrom":subQ0}),-1.0]])]});}
            var Q27;
            {var subQ0=sQuery(id+"F0.wireOp",EDGE,"E8");Q27=makeQuery(id+"F0.imprint","IMPRINT",FACE,{"disambiguationData":[TD([[makeQuery(id+"F0.imprint","IMPRINT",EDGE,{"derivedFrom":subQ0}),1.0]])]});}
            var Q28;
            {var subQ0=sQuery(id+"F0.wireOp",EDGE,"E95");var subQ4=sQuery(id+"F0.wireOp",EDGE,"E5");var subQ5=makeQuery(id+"F0.imprint","INTERSECT",VERTEX,{"derivedFrom":[subQ4,subQ0]});Q28=makeQuery(id+"F0.imprint","IMPRINT",FACE,{"disambiguationData":[TD([[makeQuery(id+"F0.imprint","IMPRINT",EDGE,{"disambiguationData":[TD([[subQ5,-1.0]])],"derivedFrom":subQ4}),1.0]])]});}
            var Q29;
            {var subQ0=sQuery(id+"F0.wireOp",EDGE,"E95");var subQ2=sQuery(id+"F0.wireOp",EDGE,"E5");var subQ3=makeQuery(id+"F0.imprint","INTERSECT",VERTEX,{"derivedFrom":[subQ2,subQ0]});Q29=makeQuery(id+"F0.imprint","IMPRINT",FACE,{"disambiguationData":[TD([[makeQuery(id+"F0.imprint","IMPRINT",EDGE,{"disambiguationData":[TD([[subQ3,-1.0]])],"derivedFrom":subQ2}),-1.0]])]});}
            var Q30;
            {var subQ3=sQuery(id+"F0.wireOp",EDGE,"E94");var subQ5=sQuery(id+"F0.wireOp",EDGE,"E12");var subQ6=makeQuery(id+"F0.imprint","INTERSECT",VERTEX,{"derivedFrom":[subQ5,subQ3]});Q30=makeQuery(id+"F0.imprint","IMPRINT",FACE,{"disambiguationData":[TD([[makeQuery(id+"F0.imprint","IMPRINT",EDGE,{"disambiguationData":[TD([[subQ6,-1.0]])],"derivedFrom":subQ5}),1.0]])]});}
            var Q31;
            {var subQ0=sQuery(id+"F0.wireOp",EDGE,"E94");var subQ1=sQuery(id+"F0.wireOp",EDGE,"E45.MirrorCS");var subQ2=makeQuery(id+"F0.imprint","INTERSECT",VERTEX,{"derivedFrom":[subQ1,subQ0]});Q31=makeQuery(id+"F0.imprint","IMPRINT",FACE,{"disambiguationData":[TD([[makeQuery(id+"F0.imprint","IMPRINT",EDGE,{"disambiguationData":[TD([[subQ2,-1.0]])],"derivedFrom":subQ1}),-1.0]])]});}
            var Q32;
            {var subQ0=sQuery(id+"F0.wireOp",EDGE,"E92");var subQ1=sQuery(id+"F0.wireOp",EDGE,"E45.MirrorCS");var subQ2=makeQuery(id+"F0.imprint","INTERSECT",VERTEX,{"derivedFrom":[subQ1,subQ0]});Q32=makeQuery(id+"F0.imprint","IMPRINT",FACE,{"disambiguationData":[TD([[makeQuery(id+"F0.imprint","IMPRINT",EDGE,{"disambiguationData":[TD([[subQ2,-1.0]])],"derivedFrom":subQ1}),-1.0]])]});}
            var Q33;
            {var subQ0=sQuery(id+"F0.wireOp",EDGE,"E92");var subQ5=sQuery(id+"F0.wireOp",EDGE,"E12");var subQ6=makeQuery(id+"F0.imprint","INTERSECT",VERTEX,{"derivedFrom":[subQ5,subQ0]});Q33=makeQuery(id+"F0.imprint","IMPRINT",FACE,{"disambiguationData":[TD([[makeQuery(id+"F0.imprint","IMPRINT",EDGE,{"disambiguationData":[TD([[subQ6,-1.0]])],"derivedFrom":subQ5}),1.0]])]});}
            var Q34;
            {var subQ3=sQuery(id+"F0.wireOp",EDGE,"E90");var subQ5=sQuery(id+"F0.wireOp",EDGE,"E12");var subQ7=makeQuery(id+"F0.imprint","INTERSECT",VERTEX,{"derivedFrom":[subQ5,subQ3]});Q34=makeQuery(id+"F0.imprint","IMPRINT",FACE,{"disambiguationData":[TD([[makeQuery(id+"F0.imprint","IMPRINT",EDGE,{"disambiguationData":[TD([[subQ7,-1.0]])],"derivedFrom":subQ5}),1.0]])]});}
            var Q35;
            {var subQ0=sQuery(id+"F0.wireOp",EDGE,"E90");var subQ1=sQuery(id+"F0.wireOp",EDGE,"E45.MirrorCS");var subQ2=makeQuery(id+"F0.imprint","INTERSECT",VERTEX,{"derivedFrom":[subQ1,subQ0]});Q35=makeQuery(id+"F0.imprint","IMPRINT",FACE,{"disambiguationData":[TD([[makeQuery(id+"F0.imprint","IMPRINT",EDGE,{"disambiguationData":[TD([[subQ2,-1.0]])],"derivedFrom":subQ1}),-1.0]])]});}
            var Q36;
            {var subQ3=sQuery(id+"F0.wireOp",EDGE,"E88");var subQ5=sQuery(id+"F0.wireOp",EDGE,"E53.MirrorCS");var subQ6=makeQuery(id+"F0.imprint","INTERSECT",VERTEX,{"derivedFrom":[subQ5,subQ3]});Q36=makeQuery(id+"F0.imprint","IMPRINT",FACE,{"disambiguationData":[TD([[makeQuery(id+"F0.imprint","IMPRINT",EDGE,{"disambiguationData":[TD([[subQ6,-1.0]])],"derivedFrom":subQ5}),1.0]])]});}
            var Q37;
            {var subQ3=sQuery(id+"F0.wireOp",EDGE,"E88");var subQ5=sQuery(id+"F0.wireOp",EDGE,"E12");var subQ7=makeQuery(id+"F0.imprint","INTERSECT",VERTEX,{"derivedFrom":[subQ5,subQ3]});Q37=makeQuery(id+"F0.imprint","IMPRINT",FACE,{"disambiguationData":[TD([[makeQuery(id+"F0.imprint","IMPRINT",EDGE,{"disambiguationData":[TD([[subQ7,-1.0]])],"derivedFrom":subQ5}),1.0]])]});}
            var Q38;
            {var subQ0=sQuery(id+"F0.wireOp",EDGE,"E85");var subQ1=sQuery(id+"F0.wireOp",EDGE,"E5");var subQ2=makeQuery(id+"F0.imprint","INTERSECT",VERTEX,{"derivedFrom":[subQ1,subQ0]});Q38=makeQuery(id+"F0.imprint","IMPRINT",FACE,{"disambiguationData":[TD([[makeQuery(id+"F0.imprint","IMPRINT",EDGE,{"disambiguationData":[TD([[subQ2,-1.0]])],"derivedFrom":subQ1}),-1.0]])]});}
            var Q39;
            {var subQ0=sQuery(id+"F0.wireOp",EDGE,"E85");var subQ1=sQuery(id+"F0.wireOp",EDGE,"E5");var subQ2=makeQuery(id+"F0.imprint","INTERSECT",VERTEX,{"derivedFrom":[subQ1,subQ0]});Q39=makeQuery(id+"F0.imprint","IMPRINT",FACE,{"disambiguationData":[TD([[makeQuery(id+"F0.imprint","IMPRINT",EDGE,{"disambiguationData":[TD([[subQ2,-1.0]])],"derivedFrom":subQ1}),1.0]])]});}
            extrude(context, id + "F2", {"entities" : qUnion([Q0, Q1, Q2, Q3, Q4, Q5, Q6, Q7, Q8, Q9, Q10, Q11, Q12, Q13, Q14, Q15, Q16, Q17, Q18, Q19, Q20, Q21, Q22, Q23, Q24, Q25, Q26, Q27, Q28, Q29, Q30, Q31, Q32, Q33, Q34, Q35, Q36, Q37, Q38, Q39]), "operationType" : NewBodyOperationType.ADD, "depth" : 10 * mm});
        }
        {
            var Q0;
            {var subQ5=sQuery(id+"F0.wireOp",EDGE,"E71");Q0=makeQuery(id+"F0.imprint","IMPRINT",FACE,{"disambiguationData":[TD([[makeQuery(id+"F0.imprint","IMPRINT",EDGE,{"derivedFrom":subQ5}),-1.0]])]});}
            var Q1;
            {var subQ0=sQuery(id+"F0.wireOp",EDGE,"E104.MirrorCS");Q1=makeQuery(id+"F0.imprint","IMPRINT",FACE,{"disambiguationData":[TD([[makeQuery(id+"F0.imprint","IMPRINT",EDGE,{"derivedFrom":subQ0}),1.0]])]});}
            var Q2;
            {var subQ5=sQuery(id+"F0.wireOp",EDGE,"E110.MirrorCS");Q2=makeQuery(id+"F0.imprint","IMPRINT",FACE,{"disambiguationData":[TD([[makeQuery(id+"F0.imprint","IMPRINT",EDGE,{"derivedFrom":subQ5}),1.0]])]});}
            var Q3;
            {var subQ0=sQuery(id+"F0.wireOp",EDGE,"E77");Q3=makeQuery(id+"F0.imprint","IMPRINT",FACE,{"disambiguationData":[TD([[makeQuery(id+"F0.imprint","IMPRINT",EDGE,{"derivedFrom":subQ0}),-1.0]])]});}
            var Q4;
            {var subQ0=sQuery(id+"F0.wireOp",EDGE,"E111.MirrorCS");var subQ1=sQuery(id+"F0.wireOp",EDGE,"E85");var subQ2=makeQuery(id+"F0.imprint","INTERSECT",VERTEX,{"derivedFrom":[subQ1,subQ0]});Q4=makeQuery(id+"F0.imprint","IMPRINT",FACE,{"disambiguationData":[TD([[makeQuery(id+"F0.imprint","IMPRINT",EDGE,{"disambiguationData":[TD([[subQ2,-1.0]])],"derivedFrom":subQ1}),-1.0]])]});}
            var Q5;
            {var subQ0=sQuery(id+"F0.wireOp",EDGE,"E101.MirrorCS");var subQ1=sQuery(id+"F0.wireOp",EDGE,"E85");var subQ2=makeQuery(id+"F0.imprint","INTERSECT",VERTEX,{"derivedFrom":[subQ1,subQ0]});Q5=makeQuery(id+"F0.imprint","IMPRINT",FACE,{"disambiguationData":[TD([[makeQuery(id+"F0.imprint","IMPRINT",EDGE,{"disambiguationData":[TD([[subQ2,-1.0]])],"derivedFrom":subQ1}),-1.0]])]});}
            var Q6;
            {var subQ5=sQuery(id+"F0.wireOp",EDGE,"E85");var subQ7=sQuery(id+"F0.wireOp",EDGE,"E103.MirrorCS");var subQ8=makeQuery(id+"F0.imprint","INTERSECT",VERTEX,{"derivedFrom":[subQ5,subQ7]});Q6=makeQuery(id+"F0.imprint","IMPRINT",FACE,{"disambiguationData":[TD([[makeQuery(id+"F0.imprint","IMPRINT",EDGE,{"disambiguationData":[TD([[subQ8,-1.0]])],"derivedFrom":subQ5}),-1.0]])]});}
            var Q7;
            {var subQ0=sQuery(id+"F0.wireOp",EDGE,"E85");var subQ3=sQuery(id+"F0.wireOp",EDGE,"E78");var subQ4=makeQuery(id+"F0.imprint","INTERSECT",VERTEX,{"derivedFrom":[subQ3,subQ0]});Q7=makeQuery(id+"F0.imprint","IMPRINT",FACE,{"disambiguationData":[TD([[makeQuery(id+"F0.imprint","IMPRINT",EDGE,{"disambiguationData":[TD([[subQ4,-1.0]])],"derivedFrom":subQ3}),1.0]])]});}
            var Q8;
            {var subQ0=sQuery(id+"F0.wireOp",EDGE,"E85");var subQ1=sQuery(id+"F0.wireOp",EDGE,"E78");var subQ2=makeQuery(id+"F0.imprint","INTERSECT",VERTEX,{"derivedFrom":[subQ1,subQ0]});Q8=makeQuery(id+"F0.imprint","IMPRINT",FACE,{"disambiguationData":[TD([[makeQuery(id+"F0.imprint","IMPRINT",EDGE,{"disambiguationData":[TD([[subQ2,-1.0]])],"derivedFrom":subQ1}),-1.0]])]});}
            var Q9;
            {var subQ0=sQuery(id+"F0.wireOp",EDGE,"E86");var subQ1=sQuery(id+"F0.wireOp",EDGE,"E70");var subQ2=makeQuery(id+"F0.imprint","INTERSECT",VERTEX,{"derivedFrom":[subQ1,subQ0]});Q9=makeQuery(id+"F0.imprint","IMPRINT",FACE,{"disambiguationData":[TD([[makeQuery(id+"F0.imprint","IMPRINT",EDGE,{"disambiguationData":[TD([[subQ2,-1.0]])],"derivedFrom":subQ1}),-1.0]])]});}
            var Q10;
            {var subQ0=sQuery(id+"F0.wireOp",EDGE,"E111.MirrorCS");var subQ1=sQuery(id+"F0.wireOp",EDGE,"E87");var subQ2=makeQuery(id+"F0.imprint","INTERSECT",VERTEX,{"derivedFrom":[subQ1,subQ0]});Q10=makeQuery(id+"F0.imprint","IMPRINT",FACE,{"disambiguationData":[TD([[makeQuery(id+"F0.imprint","IMPRINT",EDGE,{"disambiguationData":[TD([[subQ2,-1.0]])],"derivedFrom":subQ1}),-1.0]])]});}
            var Q11;
            {var subQ0=sQuery(id+"F0.wireOp",EDGE,"E101.MirrorCS");var subQ1=sQuery(id+"F0.wireOp",EDGE,"E87");var subQ2=makeQuery(id+"F0.imprint","INTERSECT",VERTEX,{"derivedFrom":[subQ1,subQ0]});Q11=makeQuery(id+"F0.imprint","IMPRINT",FACE,{"disambiguationData":[TD([[makeQuery(id+"F0.imprint","IMPRINT",EDGE,{"disambiguationData":[TD([[subQ2,-1.0]])],"derivedFrom":subQ1}),-1.0]])]});}
            var Q12;
            {var subQ0=sQuery(id+"F0.wireOp",EDGE,"E88");var subQ1=sQuery(id+"F0.wireOp",EDGE,"E76");var subQ2=makeQuery(id+"F0.imprint","INTERSECT",VERTEX,{"derivedFrom":[subQ1,subQ0]});Q12=makeQuery(id+"F0.imprint","IMPRINT",FACE,{"disambiguationData":[TD([[makeQuery(id+"F0.imprint","IMPRINT",EDGE,{"disambiguationData":[TD([[subQ2,-1.0]])],"derivedFrom":subQ1}),-1.0]])]});}
            var Q13;
            {var subQ0=sQuery(id+"F0.wireOp",EDGE,"E88");var subQ1=sQuery(id+"F0.wireOp",EDGE,"E76");var subQ2=makeQuery(id+"F0.imprint","INTERSECT",VERTEX,{"derivedFrom":[subQ1,subQ0]});Q13=makeQuery(id+"F0.imprint","IMPRINT",FACE,{"disambiguationData":[TD([[makeQuery(id+"F0.imprint","IMPRINT",EDGE,{"disambiguationData":[TD([[subQ2,-1.0]])],"derivedFrom":subQ1}),1.0]])]});}
            var Q14;
            {var subQ0=sQuery(id+"F0.wireOp",EDGE,"E87");var subQ1=sQuery(id+"F0.wireOp",EDGE,"E78");var subQ2=makeQuery(id+"F0.imprint","INTERSECT",VERTEX,{"derivedFrom":[subQ1,subQ0]});Q14=makeQuery(id+"F0.imprint","IMPRINT",FACE,{"disambiguationData":[TD([[makeQuery(id+"F0.imprint","IMPRINT",EDGE,{"disambiguationData":[TD([[subQ2,-1.0]])],"derivedFrom":subQ1}),-1.0]])]});}
            var Q15;
            {var subQ0=sQuery(id+"F0.wireOp",EDGE,"E88");var subQ1=sQuery(id+"F0.wireOp",EDGE,"E70");var subQ2=makeQuery(id+"F0.imprint","INTERSECT",VERTEX,{"derivedFrom":[subQ1,subQ0]});Q15=makeQuery(id+"F0.imprint","IMPRINT",FACE,{"disambiguationData":[TD([[makeQuery(id+"F0.imprint","IMPRINT",EDGE,{"disambiguationData":[TD([[subQ2,-1.0]])],"derivedFrom":subQ1}),-1.0]])]});}
            var Q16;
            {var subQ0=sQuery(id+"F0.wireOp",EDGE,"E111.MirrorCS");var subQ1=sQuery(id+"F0.wireOp",EDGE,"E89");var subQ2=makeQuery(id+"F0.imprint","INTERSECT",VERTEX,{"derivedFrom":[subQ1,subQ0]});Q16=makeQuery(id+"F0.imprint","IMPRINT",FACE,{"disambiguationData":[TD([[makeQuery(id+"F0.imprint","IMPRINT",EDGE,{"disambiguationData":[TD([[subQ2,-1.0]])],"derivedFrom":subQ1}),-1.0]])]});}
            var Q17;
            {var subQ0=sQuery(id+"F0.wireOp",EDGE,"E112");var subQ1=sQuery(id+"F0.wireOp",EDGE,"E89");var subQ2=makeQuery(id+"F0.imprint","INTERSECT",VERTEX,{"derivedFrom":[subQ1,subQ0]});Q17=makeQuery(id+"F0.imprint","IMPRINT",FACE,{"disambiguationData":[TD([[makeQuery(id+"F0.imprint","IMPRINT",EDGE,{"disambiguationData":[TD([[subQ2,-1.0]])],"derivedFrom":subQ1}),-1.0]])]});}
            var Q18;
            {var subQ0=sQuery(id+"F0.wireOp",EDGE,"E90");var subQ1=sQuery(id+"F0.wireOp",EDGE,"E76");var subQ2=makeQuery(id+"F0.imprint","INTERSECT",VERTEX,{"derivedFrom":[subQ1,subQ0]});Q18=makeQuery(id+"F0.imprint","IMPRINT",FACE,{"disambiguationData":[TD([[makeQuery(id+"F0.imprint","IMPRINT",EDGE,{"disambiguationData":[TD([[subQ2,-1.0]])],"derivedFrom":subQ1}),-1.0]])]});}
            var Q19;
            {var subQ0=sQuery(id+"F0.wireOp",EDGE,"E105.MirrorCS");var subQ1=sQuery(id+"F0.wireOp",EDGE,"E90");var subQ2=makeQuery(id+"F0.imprint","INTERSECT",VERTEX,{"derivedFrom":[subQ1,subQ0]});Q19=makeQuery(id+"F0.imprint","IMPRINT",FACE,{"disambiguationData":[TD([[makeQuery(id+"F0.imprint","IMPRINT",EDGE,{"disambiguationData":[TD([[subQ2,-1.0]])],"derivedFrom":subQ1}),1.0]])]});}
            var Q20;
            {var subQ3=sQuery(id+"F0.wireOp",EDGE,"E90");var subQ5=sQuery(id+"F0.wireOp",EDGE,"E76");var subQ6=makeQuery(id+"F0.imprint","INTERSECT",VERTEX,{"derivedFrom":[subQ5,subQ3]});Q20=makeQuery(id+"F0.imprint","IMPRINT",FACE,{"disambiguationData":[TD([[makeQuery(id+"F0.imprint","IMPRINT",EDGE,{"disambiguationData":[TD([[subQ6,-1.0]])],"derivedFrom":subQ5}),1.0]])]});}
            var Q21;
            {var subQ0=sQuery(id+"F0.wireOp",EDGE,"E82");var subQ1=sQuery(id+"F0.wireOp",EDGE,"E81");var subQ2=makeQuery(id+"F0.imprint","INTERSECT",VERTEX,{"derivedFrom":[subQ1,subQ0]});Q21=makeQuery(id+"F0.imprint","IMPRINT",FACE,{"disambiguationData":[TD([[makeQuery(id+"F0.imprint","IMPRINT",EDGE,{"disambiguationData":[TD([[subQ2,1.0]])],"derivedFrom":subQ1}),-1.0]])]});}
            var Q22;
            {var subQ0=sQuery(id+"F0.wireOp",EDGE,"E90");var subQ1=sQuery(id+"F0.wireOp",EDGE,"E70");var subQ2=makeQuery(id+"F0.imprint","INTERSECT",VERTEX,{"derivedFrom":[subQ1,subQ0]});Q22=makeQuery(id+"F0.imprint","IMPRINT",FACE,{"disambiguationData":[TD([[makeQuery(id+"F0.imprint","IMPRINT",EDGE,{"disambiguationData":[TD([[subQ2,-1.0]])],"derivedFrom":subQ1}),-1.0]])]});}
            var Q23;
            {var subQ0=sQuery(id+"F0.wireOp",EDGE,"E112");var subQ1=sQuery(id+"F0.wireOp",EDGE,"E91");var subQ2=makeQuery(id+"F0.imprint","INTERSECT",VERTEX,{"derivedFrom":[subQ1,subQ0]});Q23=makeQuery(id+"F0.imprint","IMPRINT",FACE,{"disambiguationData":[TD([[makeQuery(id+"F0.imprint","IMPRINT",EDGE,{"disambiguationData":[TD([[subQ2,-1.0]])],"derivedFrom":subQ1}),-1.0]])]});}
            var Q24;
            {var subQ0=sQuery(id+"F0.wireOp",EDGE,"E111.MirrorCS");var subQ1=sQuery(id+"F0.wireOp",EDGE,"E91");var subQ2=makeQuery(id+"F0.imprint","INTERSECT",VERTEX,{"derivedFrom":[subQ1,subQ0]});Q24=makeQuery(id+"F0.imprint","IMPRINT",FACE,{"disambiguationData":[TD([[makeQuery(id+"F0.imprint","IMPRINT",EDGE,{"disambiguationData":[TD([[subQ2,-1.0]])],"derivedFrom":subQ1}),-1.0]])]});}
            var Q25;
            {var subQ0=sQuery(id+"F0.wireOp",EDGE,"E107.MirrorCS");var subQ1=sQuery(id+"F0.wireOp",EDGE,"E91");var subQ2=makeQuery(id+"F0.imprint","INTERSECT",VERTEX,{"derivedFrom":[subQ1,subQ0]});Q25=makeQuery(id+"F0.imprint","IMPRINT",FACE,{"disambiguationData":[TD([[makeQuery(id+"F0.imprint","IMPRINT",EDGE,{"disambiguationData":[TD([[subQ2,-1.0]])],"derivedFrom":subQ1}),-1.0]])]});}
            var Q26;
            {var subQ7=sQuery(id+"F0.wireOp",EDGE,"E105.MirrorCS");var subQ8=sQuery(id+"F0.wireOp",EDGE,"E91");var subQ9=makeQuery(id+"F0.imprint","INTERSECT",VERTEX,{"derivedFrom":[subQ8,subQ7]});Q26=makeQuery(id+"F0.imprint","IMPRINT",FACE,{"disambiguationData":[TD([[makeQuery(id+"F0.imprint","IMPRINT",EDGE,{"disambiguationData":[TD([[subQ9,-1.0]])],"derivedFrom":subQ8}),-1.0]])]});}
            var Q27;
            {var subQ0=sQuery(id+"F0.wireOp",EDGE,"E92");var subQ1=sQuery(id+"F0.wireOp",EDGE,"E76");var subQ2=makeQuery(id+"F0.imprint","INTERSECT",VERTEX,{"derivedFrom":[subQ1,subQ0]});Q27=makeQuery(id+"F0.imprint","IMPRINT",FACE,{"disambiguationData":[TD([[makeQuery(id+"F0.imprint","IMPRINT",EDGE,{"disambiguationData":[TD([[subQ2,-1.0]])],"derivedFrom":subQ1}),-1.0]])]});}
            var Q28;
            {var subQ8=sQuery(id+"F0.wireOp",EDGE,"E75");var subQ9=sQuery(id+"F0.wireOp",EDGE,"E74");var subQ10=makeQuery(id+"F0.imprint","INTERSECT",VERTEX,{"derivedFrom":[subQ9,subQ8]});Q28=makeQuery(id+"F0.imprint","IMPRINT",FACE,{"disambiguationData":[TD([[makeQuery(id+"F0.imprint","IMPRINT",EDGE,{"disambiguationData":[TD([[subQ10,1.0]])],"derivedFrom":subQ9}),-1.0]])]});}
            var Q29;
            {var subQ0=sQuery(id+"F0.wireOp",EDGE,"E91");var subQ1=sQuery(id+"F0.wireOp",EDGE,"E79");var subQ2=makeQuery(id+"F0.imprint","INTERSECT",VERTEX,{"derivedFrom":[subQ1,subQ0]});Q29=makeQuery(id+"F0.imprint","IMPRINT",FACE,{"disambiguationData":[TD([[makeQuery(id+"F0.imprint","IMPRINT",EDGE,{"disambiguationData":[TD([[subQ2,-1.0]])],"derivedFrom":subQ1}),1.0]])]});}
            var Q30;
            {var subQ0=sQuery(id+"F0.wireOp",EDGE,"E92");var subQ1=sQuery(id+"F0.wireOp",EDGE,"E70");var subQ2=makeQuery(id+"F0.imprint","INTERSECT",VERTEX,{"derivedFrom":[subQ1,subQ0]});Q30=makeQuery(id+"F0.imprint","IMPRINT",FACE,{"disambiguationData":[TD([[makeQuery(id+"F0.imprint","IMPRINT",EDGE,{"disambiguationData":[TD([[subQ2,-1.0]])],"derivedFrom":subQ1}),-1.0]])]});}
            var Q31;
            {var subQ0=sQuery(id+"F0.wireOp",EDGE,"E111.MirrorCS");var subQ1=sQuery(id+"F0.wireOp",EDGE,"E93");var subQ2=makeQuery(id+"F0.imprint","INTERSECT",VERTEX,{"derivedFrom":[subQ1,subQ0]});Q31=makeQuery(id+"F0.imprint","IMPRINT",FACE,{"disambiguationData":[TD([[makeQuery(id+"F0.imprint","IMPRINT",EDGE,{"disambiguationData":[TD([[subQ2,-1.0]])],"derivedFrom":subQ1}),-1.0]])]});}
            var Q32;
            {var subQ0=sQuery(id+"F0.wireOp",EDGE,"E107.MirrorCS");var subQ1=sQuery(id+"F0.wireOp",EDGE,"E93");var subQ2=makeQuery(id+"F0.imprint","INTERSECT",VERTEX,{"derivedFrom":[subQ1,subQ0]});Q32=makeQuery(id+"F0.imprint","IMPRINT",FACE,{"disambiguationData":[TD([[makeQuery(id+"F0.imprint","IMPRINT",EDGE,{"disambiguationData":[TD([[subQ2,-1.0]])],"derivedFrom":subQ1}),-1.0]])]});}
            var Q33;
            {var subQ0=sQuery(id+"F0.wireOp",EDGE,"E112");var subQ1=sQuery(id+"F0.wireOp",EDGE,"E93");var subQ2=makeQuery(id+"F0.imprint","INTERSECT",VERTEX,{"derivedFrom":[subQ1,subQ0]});Q33=makeQuery(id+"F0.imprint","IMPRINT",FACE,{"disambiguationData":[TD([[makeQuery(id+"F0.imprint","IMPRINT",EDGE,{"disambiguationData":[TD([[subQ2,-1.0]])],"derivedFrom":subQ1}),-1.0]])]});}
            var Q34;
            {var subQ0=sQuery(id+"F0.wireOp",EDGE,"E100.MirrorCS");var subQ1=sQuery(id+"F0.wireOp",EDGE,"E93");var subQ2=makeQuery(id+"F0.imprint","INTERSECT",VERTEX,{"derivedFrom":[subQ1,subQ0]});Q34=makeQuery(id+"F0.imprint","IMPRINT",FACE,{"disambiguationData":[TD([[makeQuery(id+"F0.imprint","IMPRINT",EDGE,{"disambiguationData":[TD([[subQ2,-1.0]])],"derivedFrom":subQ1}),-1.0]])]});}
            var Q35;
            {var subQ0=sQuery(id+"F0.wireOp",EDGE,"E105.MirrorCS");var subQ1=sQuery(id+"F0.wireOp",EDGE,"E93");var subQ2=makeQuery(id+"F0.imprint","INTERSECT",VERTEX,{"derivedFrom":[subQ1,subQ0]});Q35=makeQuery(id+"F0.imprint","IMPRINT",FACE,{"disambiguationData":[TD([[makeQuery(id+"F0.imprint","IMPRINT",EDGE,{"disambiguationData":[TD([[subQ2,-1.0]])],"derivedFrom":subQ1}),-1.0]])]});}
            var Q36;
            {var subQ0=sQuery(id+"F0.wireOp",EDGE,"E94");var subQ1=sQuery(id+"F0.wireOp",EDGE,"E76");var subQ2=makeQuery(id+"F0.imprint","INTERSECT",VERTEX,{"derivedFrom":[subQ1,subQ0]});Q36=makeQuery(id+"F0.imprint","IMPRINT",FACE,{"disambiguationData":[TD([[makeQuery(id+"F0.imprint","IMPRINT",EDGE,{"disambiguationData":[TD([[subQ2,-1.0]])],"derivedFrom":subQ1}),1.0]])]});}
            var Q37;
            {var subQ0=sQuery(id+"F0.wireOp",EDGE,"E94");var subQ1=sQuery(id+"F0.wireOp",EDGE,"E74");var subQ2=makeQuery(id+"F0.imprint","INTERSECT",VERTEX,{"derivedFrom":[subQ1,subQ0]});Q37=makeQuery(id+"F0.imprint","IMPRINT",FACE,{"disambiguationData":[TD([[makeQuery(id+"F0.imprint","IMPRINT",EDGE,{"disambiguationData":[TD([[subQ2,-1.0]])],"derivedFrom":subQ1}),-1.0]])]});}
            var Q38;
            {var subQ0=sQuery(id+"F0.wireOp",EDGE,"E93");var subQ1=sQuery(id+"F0.wireOp",EDGE,"E75");var subQ2=makeQuery(id+"F0.imprint","INTERSECT",VERTEX,{"derivedFrom":[subQ1,subQ0]});Q38=makeQuery(id+"F0.imprint","IMPRINT",FACE,{"disambiguationData":[TD([[makeQuery(id+"F0.imprint","IMPRINT",EDGE,{"disambiguationData":[TD([[subQ2,-1.0]])],"derivedFrom":subQ1}),-1.0]])]});}
            var Q39;
            {var subQ0=sQuery(id+"F0.wireOp",EDGE,"E93");var subQ1=sQuery(id+"F0.wireOp",EDGE,"E79");var subQ2=makeQuery(id+"F0.imprint","INTERSECT",VERTEX,{"derivedFrom":[subQ1,subQ0]});Q39=makeQuery(id+"F0.imprint","IMPRINT",FACE,{"disambiguationData":[TD([[makeQuery(id+"F0.imprint","IMPRINT",EDGE,{"disambiguationData":[TD([[subQ2,-1.0]])],"derivedFrom":subQ1}),1.0]])]});}
            var Q40;
            {var subQ0=sQuery(id+"F0.wireOp",EDGE,"E94");var subQ1=sQuery(id+"F0.wireOp",EDGE,"E70");var subQ2=makeQuery(id+"F0.imprint","INTERSECT",VERTEX,{"derivedFrom":[subQ1,subQ0]});Q40=makeQuery(id+"F0.imprint","IMPRINT",FACE,{"disambiguationData":[TD([[makeQuery(id+"F0.imprint","IMPRINT",EDGE,{"disambiguationData":[TD([[subQ2,-1.0]])],"derivedFrom":subQ1}),-1.0]])]});}
            var Q41;
            {var subQ0=sQuery(id+"F0.wireOp",EDGE,"E111.MirrorCS");var subQ1=sQuery(id+"F0.wireOp",EDGE,"E95");var subQ2=makeQuery(id+"F0.imprint","INTERSECT",VERTEX,{"derivedFrom":[subQ1,subQ0]});Q41=makeQuery(id+"F0.imprint","IMPRINT",FACE,{"disambiguationData":[TD([[makeQuery(id+"F0.imprint","IMPRINT",EDGE,{"disambiguationData":[TD([[subQ2,-1.0]])],"derivedFrom":subQ1}),-1.0]])]});}
            var Q42;
            {var subQ0=sQuery(id+"F0.wireOp",EDGE,"E107.MirrorCS");var subQ1=sQuery(id+"F0.wireOp",EDGE,"E95");var subQ2=makeQuery(id+"F0.imprint","INTERSECT",VERTEX,{"derivedFrom":[subQ1,subQ0]});Q42=makeQuery(id+"F0.imprint","IMPRINT",FACE,{"disambiguationData":[TD([[makeQuery(id+"F0.imprint","IMPRINT",EDGE,{"disambiguationData":[TD([[subQ2,-1.0]])],"derivedFrom":subQ1}),-1.0]])]});}
            var Q43;
            {var subQ0=sQuery(id+"F0.wireOp",EDGE,"E100.MirrorCS");var subQ1=sQuery(id+"F0.wireOp",EDGE,"E95");var subQ2=makeQuery(id+"F0.imprint","INTERSECT",VERTEX,{"derivedFrom":[subQ1,subQ0]});Q43=makeQuery(id+"F0.imprint","IMPRINT",FACE,{"disambiguationData":[TD([[makeQuery(id+"F0.imprint","IMPRINT",EDGE,{"disambiguationData":[TD([[subQ2,-1.0]])],"derivedFrom":subQ1}),-1.0]])]});}
            var Q44;
            {var subQ0=sQuery(id+"F0.wireOp",EDGE,"E99.MirrorCS");Q44=makeQuery(id+"F0.imprint","IMPRINT",FACE,{"disambiguationData":[TD([[makeQuery(id+"F0.imprint","IMPRINT",EDGE,{"derivedFrom":subQ0}),1.0]])]});}
            var Q45;
            {var subQ0=sQuery(id+"F0.wireOp",EDGE,"E83");Q45=makeQuery(id+"F0.imprint","IMPRINT",FACE,{"disambiguationData":[TD([[makeQuery(id+"F0.imprint","IMPRINT",EDGE,{"derivedFrom":subQ0}),-1.0]])]});}
            var Q46;
            {var subQ0=sQuery(id+"F0.wireOp",EDGE,"E95");var subQ1=sQuery(id+"F0.wireOp",EDGE,"E75");var subQ2=makeQuery(id+"F0.imprint","INTERSECT",VERTEX,{"derivedFrom":[subQ1,subQ0]});Q46=makeQuery(id+"F0.imprint","IMPRINT",FACE,{"disambiguationData":[TD([[makeQuery(id+"F0.imprint","IMPRINT",EDGE,{"disambiguationData":[TD([[subQ2,-1.0]])],"derivedFrom":subQ1}),-1.0]])]});}
            var Q47;
            {var subQ0=sQuery(id+"F0.wireOp",EDGE,"E95");var subQ1=sQuery(id+"F0.wireOp",EDGE,"E79");var subQ2=makeQuery(id+"F0.imprint","INTERSECT",VERTEX,{"derivedFrom":[subQ1,subQ0]});Q47=makeQuery(id+"F0.imprint","IMPRINT",FACE,{"disambiguationData":[TD([[makeQuery(id+"F0.imprint","IMPRINT",EDGE,{"disambiguationData":[TD([[subQ2,-1.0]])],"derivedFrom":subQ1}),1.0]])]});}
            var Q48;
            {var subQ0=sQuery(id+"F0.wireOp",EDGE,"E96");var subQ1=sQuery(id+"F0.wireOp",EDGE,"E70");var subQ2=makeQuery(id+"F0.imprint","INTERSECT",VERTEX,{"derivedFrom":[subQ1,subQ0]});Q48=makeQuery(id+"F0.imprint","IMPRINT",FACE,{"disambiguationData":[TD([[makeQuery(id+"F0.imprint","IMPRINT",EDGE,{"disambiguationData":[TD([[subQ2,-1.0]])],"derivedFrom":subQ1}),-1.0]])]});}
            var Q49;
            {var subQ0=sQuery(id+"F0.wireOp",EDGE,"E108.MirrorCS");Q49=makeQuery(id+"F0.imprint","IMPRINT",FACE,{"disambiguationData":[TD([[makeQuery(id+"F0.imprint","IMPRINT",EDGE,{"derivedFrom":subQ0}),1.0]])]});}
            var Q50;
            {var subQ0=sQuery(id+"F0.wireOp",EDGE,"E97");var subQ1=sQuery(id+"F0.wireOp",EDGE,"E76");var subQ2=makeQuery(id+"F0.imprint","INTERSECT",VERTEX,{"derivedFrom":[subQ1,subQ0]});Q50=makeQuery(id+"F0.imprint","IMPRINT",FACE,{"disambiguationData":[TD([[makeQuery(id+"F0.imprint","IMPRINT",EDGE,{"disambiguationData":[TD([[subQ2,-1.0]])],"derivedFrom":subQ1}),-1.0]])]});}
            var Q51;
            {var subQ0=sQuery(id+"F0.wireOp",EDGE,"E97");var subQ1=sQuery(id+"F0.wireOp",EDGE,"E74");var subQ2=makeQuery(id+"F0.imprint","INTERSECT",VERTEX,{"derivedFrom":[subQ1,subQ0]});Q51=makeQuery(id+"F0.imprint","IMPRINT",FACE,{"disambiguationData":[TD([[makeQuery(id+"F0.imprint","IMPRINT",EDGE,{"disambiguationData":[TD([[subQ2,-1.0]])],"derivedFrom":subQ1}),-1.0]])]});}
            var Q52;
            {var subQ0=sQuery(id+"F0.wireOp",EDGE,"E73");Q52=makeQuery(id+"F0.imprint","IMPRINT",FACE,{"disambiguationData":[TD([[makeQuery(id+"F0.imprint","IMPRINT",EDGE,{"derivedFrom":subQ0}),-1.0]])]});}
            var Q53;
            {var subQ0=sQuery(id+"F0.wireOp",EDGE,"E98.MirrorCS");Q53=makeQuery(id+"F0.imprint","IMPRINT",FACE,{"disambiguationData":[TD([[makeQuery(id+"F0.imprint","IMPRINT",EDGE,{"derivedFrom":subQ0}),1.0]])]});}
            var Q54;
            {var subQ10=sQuery(id+"F0.wireOp",EDGE,"E80");Q54=makeQuery(id+"F0.imprint","IMPRINT",FACE,{"disambiguationData":[TD([[makeQuery(id+"F0.imprint","IMPRINT",EDGE,{"derivedFrom":subQ10}),-1.0]])]});}
            var Q55;
            {var subQ0=sQuery(id+"F0.wireOp",EDGE,"E80");Q55=makeQuery(id+"F0.imprint","IMPRINT",FACE,{"disambiguationData":[TD([[makeQuery(id+"F0.imprint","IMPRINT",EDGE,{"derivedFrom":subQ0}),1.0]])]});}
            var Q56;
            {var subQ5=sQuery(id+"F0.wireOp",EDGE,"E109.MirrorCS");Q56=makeQuery(id+"F0.imprint","IMPRINT",FACE,{"disambiguationData":[TD([[makeQuery(id+"F0.imprint","IMPRINT",EDGE,{"derivedFrom":subQ5}),-1.0]])]});}
            var Q57;
            {var subQ0=sQuery(id+"F0.wireOp",EDGE,"E94");var subQ1=sQuery(id+"F0.wireOp",EDGE,"E76");var subQ2=makeQuery(id+"F0.imprint","INTERSECT",VERTEX,{"derivedFrom":[subQ1,subQ0]});Q57=makeQuery(id+"F0.imprint","IMPRINT",FACE,{"disambiguationData":[TD([[makeQuery(id+"F0.imprint","IMPRINT",EDGE,{"disambiguationData":[TD([[subQ2,-1.0]])],"derivedFrom":subQ1}),-1.0]])]});}
            var Q58;
            {var subQ0=sQuery(id+"F0.wireOp",EDGE,"E99.MirrorCS");Q58=makeQuery(id+"F0.imprint","IMPRINT",FACE,{"disambiguationData":[TD([[makeQuery(id+"F0.imprint","IMPRINT",EDGE,{"derivedFrom":subQ0}),-1.0]])]});}
            var Q59;
            {var subQ0=sQuery(id+"F0.wireOp",EDGE,"E83");Q59=makeQuery(id+"F0.imprint","IMPRINT",FACE,{"disambiguationData":[TD([[makeQuery(id+"F0.imprint","IMPRINT",EDGE,{"derivedFrom":subQ0}),1.0]])]});}
            var Q60;
            {var subQ0=sQuery(id+"F0.wireOp",EDGE,"E92");var subQ1=sQuery(id+"F0.wireOp",EDGE,"E76");var subQ2=makeQuery(id+"F0.imprint","INTERSECT",VERTEX,{"derivedFrom":[subQ1,subQ0]});Q60=makeQuery(id+"F0.imprint","IMPRINT",FACE,{"disambiguationData":[TD([[makeQuery(id+"F0.imprint","IMPRINT",EDGE,{"disambiguationData":[TD([[subQ2,-1.0]])],"derivedFrom":subQ1}),1.0]])]});}
            var Q61;
            {var subQ0=sQuery(id+"F0.wireOp",EDGE,"E69");var subQ1=sQuery(id+"F0.wireOp",EDGE,"E56.MirrorCS");var subQ2=makeQuery(id+"F0.imprint","INTERSECT",VERTEX,{"derivedFrom":[subQ1,subQ0]});Q61=makeQuery(id+"F0.imprint","IMPRINT",FACE,{"disambiguationData":[TD([[makeQuery(id+"F0.imprint","IMPRINT",EDGE,{"disambiguationData":[TD([[subQ2,-1.0]])],"derivedFrom":subQ1}),1.0]])]});}
            extrude(context, id + "F3", {"entities" : qUnion([Q0, Q1, Q2, Q3, Q4, Q5, Q6, Q7, Q8, Q9, Q10, Q11, Q12, Q13, Q14, Q15, Q16, Q17, Q18, Q19, Q20, Q21, Q22, Q23, Q24, Q25, Q26, Q27, Q28, Q29, Q30, Q31, Q32, Q33, Q34, Q35, Q36, Q37, Q38, Q39, Q40, Q41, Q42, Q43, Q44, Q45, Q46, Q47, Q48, Q49, Q50, Q51, Q52, Q53, Q54, Q55, Q56, Q57, Q58, Q59, Q60, Q61]), "operationType" : NewBodyOperationType.ADD, "depth" : 10 * mm});
        }
        {
            var Q0;
            {var subQ1=sQuery(id+"F0.wireOp",EDGE,"E84");var subQ4=sQuery(id+"F0.wireOp",EDGE,"E117");var subQ6=makeQuery(id+"F0.imprint","INTERSECT",VERTEX,{"derivedFrom":[subQ1,subQ4]});Q0=makeQuery(id+"F0.imprint","IMPRINT",FACE,{"disambiguationData":[TD([[makeQuery(id+"F0.imprint","IMPRINT",EDGE,{"disambiguationData":[TD([[subQ6,-1.0]])],"derivedFrom":subQ1}),1.0]])]});}
            var Q1;
            {var subQ0=sQuery(id+"F0.wireOp",EDGE,"E118");var subQ1=sQuery(id+"F0.wireOp",EDGE,"E85");var subQ2=makeQuery(id+"F0.imprint","INTERSECT",VERTEX,{"disambiguationData":[OD(1.0)],"derivedFrom":[subQ1,subQ0]});Q1=makeQuery(id+"F0.imprint","IMPRINT",FACE,{"disambiguationData":[TD([[makeQuery(id+"F0.imprint","IMPRINT",EDGE,{"disambiguationData":[TD([[subQ2,-1.0]])],"derivedFrom":subQ1}),-1.0]])]});}
            var Q2;
            {var subQ0=sQuery(id+"F0.wireOp",EDGE,"E121.2");var subQ1=sQuery(id+"F0.wireOp",EDGE,"E85");var subQ2=makeQuery(id+"F0.imprint","INTERSECT",VERTEX,{"disambiguationData":[OD(0.0)],"derivedFrom":[subQ1,subQ0]});Q2=makeQuery(id+"F0.imprint","IMPRINT",FACE,{"disambiguationData":[TD([[makeQuery(id+"F0.imprint","IMPRINT",EDGE,{"disambiguationData":[TD([[subQ2,-1.0]])],"derivedFrom":subQ1}),-1.0]])]});}
            var Q3;
            {var subQ0=sQuery(id+"F0.wireOp",EDGE,"E121.0");var subQ1=sQuery(id+"F0.wireOp",EDGE,"E85");var subQ2=makeQuery(id+"F0.imprint","INTERSECT",VERTEX,{"derivedFrom":[subQ1,subQ0]});Q3=makeQuery(id+"F0.imprint","IMPRINT",FACE,{"disambiguationData":[TD([[makeQuery(id+"F0.imprint","IMPRINT",EDGE,{"disambiguationData":[TD([[subQ2,-1.0]])],"derivedFrom":subQ1}),-1.0]])]});}
            var Q4;
            {var subQ0=sQuery(id+"F0.wireOp",EDGE,"E117");var subQ1=sQuery(id+"F0.wireOp",EDGE,"E85");var subQ2=makeQuery(id+"F0.imprint","INTERSECT",VERTEX,{"derivedFrom":[subQ1,subQ0]});Q4=makeQuery(id+"F0.imprint","IMPRINT",FACE,{"disambiguationData":[TD([[makeQuery(id+"F0.imprint","IMPRINT",EDGE,{"disambiguationData":[TD([[subQ2,-1.0]])],"derivedFrom":subQ1}),-1.0]])]});}
            var Q5;
            {var subQ0=sQuery(id+"F0.wireOp",EDGE,"E115.MirrorCS");var subQ1=sQuery(id+"F0.wireOp",EDGE,"E87");var subQ2=makeQuery(id+"F0.imprint","INTERSECT",VERTEX,{"derivedFrom":[subQ1,subQ0]});Q5=makeQuery(id+"F0.imprint","IMPRINT",FACE,{"disambiguationData":[TD([[makeQuery(id+"F0.imprint","IMPRINT",EDGE,{"disambiguationData":[TD([[subQ2,-1.0]])],"derivedFrom":subQ1}),-1.0]])]});}
            var Q6;
            {var subQ0=sQuery(id+"F0.wireOp",EDGE,"E121.0");var subQ1=sQuery(id+"F0.wireOp",EDGE,"E87");var subQ2=makeQuery(id+"F0.imprint","INTERSECT",VERTEX,{"derivedFrom":[subQ1,subQ0]});Q6=makeQuery(id+"F0.imprint","IMPRINT",FACE,{"disambiguationData":[TD([[makeQuery(id+"F0.imprint","IMPRINT",EDGE,{"disambiguationData":[TD([[subQ2,-1.0]])],"derivedFrom":subQ1}),-1.0]])]});}
            var Q7;
            {var subQ0=sQuery(id+"F0.wireOp",EDGE,"E121.2");var subQ1=sQuery(id+"F0.wireOp",EDGE,"E87");var subQ2=makeQuery(id+"F0.imprint","INTERSECT",VERTEX,{"derivedFrom":[subQ1,subQ0]});Q7=makeQuery(id+"F0.imprint","IMPRINT",FACE,{"disambiguationData":[TD([[makeQuery(id+"F0.imprint","IMPRINT",EDGE,{"disambiguationData":[TD([[subQ2,-1.0]])],"derivedFrom":subQ1}),-1.0]])]});}
            var Q8;
            {var subQ0=sQuery(id+"F0.wireOp",EDGE,"E120");var subQ1=sQuery(id+"F0.wireOp",EDGE,"E87");var subQ2=makeQuery(id+"F0.imprint","INTERSECT",VERTEX,{"derivedFrom":[subQ1,subQ0]});Q8=makeQuery(id+"F0.imprint","IMPRINT",FACE,{"disambiguationData":[TD([[makeQuery(id+"F0.imprint","IMPRINT",EDGE,{"disambiguationData":[TD([[subQ2,1.0]])],"derivedFrom":subQ1}),-1.0]])]});}
            var Q9;
            {var subQ0=sQuery(id+"F0.wireOp",EDGE,"E118");var subQ1=sQuery(id+"F0.wireOp",EDGE,"E89");var subQ2=makeQuery(id+"F0.imprint","INTERSECT",VERTEX,{"derivedFrom":[subQ1,subQ0]});Q9=makeQuery(id+"F0.imprint","IMPRINT",FACE,{"disambiguationData":[TD([[makeQuery(id+"F0.imprint","IMPRINT",EDGE,{"disambiguationData":[TD([[subQ2,1.0]])],"derivedFrom":subQ1}),-1.0]])]});}
            var Q10;
            {var subQ0=sQuery(id+"F0.wireOp",EDGE,"E121.0");var subQ1=sQuery(id+"F0.wireOp",EDGE,"E89");var subQ2=makeQuery(id+"F0.imprint","INTERSECT",VERTEX,{"derivedFrom":[subQ1,subQ0]});Q10=makeQuery(id+"F0.imprint","IMPRINT",FACE,{"disambiguationData":[TD([[makeQuery(id+"F0.imprint","IMPRINT",EDGE,{"disambiguationData":[TD([[subQ2,-1.0]])],"derivedFrom":subQ1}),-1.0]])]});}
            var Q11;
            {var subQ0=sQuery(id+"F0.wireOp",EDGE,"E117");var subQ1=sQuery(id+"F0.wireOp",EDGE,"E89");var subQ2=makeQuery(id+"F0.imprint","INTERSECT",VERTEX,{"derivedFrom":[subQ1,subQ0]});Q11=makeQuery(id+"F0.imprint","IMPRINT",FACE,{"disambiguationData":[TD([[makeQuery(id+"F0.imprint","IMPRINT",EDGE,{"disambiguationData":[TD([[subQ2,-1.0]])],"derivedFrom":subQ1}),-1.0]])]});}
            var Q12;
            {var subQ0=sQuery(id+"F0.wireOp",EDGE,"E117");var subQ1=sQuery(id+"F0.wireOp",EDGE,"E91");var subQ2=makeQuery(id+"F0.imprint","INTERSECT",VERTEX,{"derivedFrom":[subQ1,subQ0]});Q12=makeQuery(id+"F0.imprint","IMPRINT",FACE,{"disambiguationData":[TD([[makeQuery(id+"F0.imprint","IMPRINT",EDGE,{"disambiguationData":[TD([[subQ2,-1.0]])],"derivedFrom":subQ1}),-1.0]])]});}
            var Q13;
            {var subQ0=sQuery(id+"F0.wireOp",EDGE,"E121.0");var subQ1=sQuery(id+"F0.wireOp",EDGE,"E91");var subQ2=makeQuery(id+"F0.imprint","INTERSECT",VERTEX,{"derivedFrom":[subQ1,subQ0]});Q13=makeQuery(id+"F0.imprint","IMPRINT",FACE,{"disambiguationData":[TD([[makeQuery(id+"F0.imprint","IMPRINT",EDGE,{"disambiguationData":[TD([[subQ2,-1.0]])],"derivedFrom":subQ1}),-1.0]])]});}
            var Q14;
            {var subQ0=sQuery(id+"F0.wireOp",EDGE,"E118");var subQ1=sQuery(id+"F0.wireOp",EDGE,"E91");var subQ2=makeQuery(id+"F0.imprint","INTERSECT",VERTEX,{"derivedFrom":[subQ1,subQ0]});Q14=makeQuery(id+"F0.imprint","IMPRINT",FACE,{"disambiguationData":[TD([[makeQuery(id+"F0.imprint","IMPRINT",EDGE,{"disambiguationData":[TD([[subQ2,1.0]])],"derivedFrom":subQ1}),-1.0]])]});}
            var Q15;
            {var subQ0=sQuery(id+"F0.wireOp",EDGE,"E118");var subQ1=sQuery(id+"F0.wireOp",EDGE,"E93");var subQ2=makeQuery(id+"F0.imprint","INTERSECT",VERTEX,{"derivedFrom":[subQ1,subQ0]});Q15=makeQuery(id+"F0.imprint","IMPRINT",FACE,{"disambiguationData":[TD([[makeQuery(id+"F0.imprint","IMPRINT",EDGE,{"disambiguationData":[TD([[subQ2,1.0]])],"derivedFrom":subQ1}),-1.0]])]});}
            var Q16;
            {var subQ0=sQuery(id+"F0.wireOp",EDGE,"E121.0");var subQ1=sQuery(id+"F0.wireOp",EDGE,"E93");var subQ2=makeQuery(id+"F0.imprint","INTERSECT",VERTEX,{"derivedFrom":[subQ1,subQ0]});Q16=makeQuery(id+"F0.imprint","IMPRINT",FACE,{"disambiguationData":[TD([[makeQuery(id+"F0.imprint","IMPRINT",EDGE,{"disambiguationData":[TD([[subQ2,-1.0]])],"derivedFrom":subQ1}),-1.0]])]});}
            var Q17;
            {var subQ0=sQuery(id+"F0.wireOp",EDGE,"E117");var subQ1=sQuery(id+"F0.wireOp",EDGE,"E93");var subQ2=makeQuery(id+"F0.imprint","INTERSECT",VERTEX,{"derivedFrom":[subQ1,subQ0]});Q17=makeQuery(id+"F0.imprint","IMPRINT",FACE,{"disambiguationData":[TD([[makeQuery(id+"F0.imprint","IMPRINT",EDGE,{"disambiguationData":[TD([[subQ2,-1.0]])],"derivedFrom":subQ1}),-1.0]])]});}
            var Q18;
            {var subQ0=sQuery(id+"F0.wireOp",EDGE,"E117");var subQ1=sQuery(id+"F0.wireOp",EDGE,"E95");var subQ2=makeQuery(id+"F0.imprint","INTERSECT",VERTEX,{"disambiguationData":[OD(1.0)],"derivedFrom":[subQ1,subQ0]});Q18=makeQuery(id+"F0.imprint","IMPRINT",FACE,{"disambiguationData":[TD([[makeQuery(id+"F0.imprint","IMPRINT",EDGE,{"disambiguationData":[TD([[subQ2,-1.0]])],"derivedFrom":subQ1}),-1.0]])]});}
            var Q19;
            {var subQ0=sQuery(id+"F0.wireOp",EDGE,"E121.0");var subQ1=sQuery(id+"F0.wireOp",EDGE,"E95");var subQ2=makeQuery(id+"F0.imprint","INTERSECT",VERTEX,{"derivedFrom":[subQ1,subQ0]});Q19=makeQuery(id+"F0.imprint","IMPRINT",FACE,{"disambiguationData":[TD([[makeQuery(id+"F0.imprint","IMPRINT",EDGE,{"disambiguationData":[TD([[subQ2,-1.0]])],"derivedFrom":subQ1}),-1.0]])]});}
            var Q20;
            {var subQ0=sQuery(id+"F0.wireOp",EDGE,"E118");var subQ1=sQuery(id+"F0.wireOp",EDGE,"E95");var subQ2=makeQuery(id+"F0.imprint","INTERSECT",VERTEX,{"derivedFrom":[subQ1,subQ0]});Q20=makeQuery(id+"F0.imprint","IMPRINT",FACE,{"disambiguationData":[TD([[makeQuery(id+"F0.imprint","IMPRINT",EDGE,{"disambiguationData":[TD([[subQ2,1.0]])],"derivedFrom":subQ1}),-1.0]])]});}
            var Q21;
            {var subQ1=sQuery(id+"F0.wireOp",EDGE,"E97");var subQ8=sQuery(id+"F0.wireOp",EDGE,"E119");var subQ9=makeQuery(id+"F0.imprint","INTERSECT",VERTEX,{"derivedFrom":[subQ1,subQ8]});Q21=makeQuery(id+"F0.imprint","IMPRINT",FACE,{"disambiguationData":[TD([[makeQuery(id+"F0.imprint","IMPRINT",EDGE,{"disambiguationData":[TD([[subQ9,-1.0]])],"derivedFrom":subQ1}),-1.0]])]});}
            var Q22;
            {var subQ1=sQuery(id+"F0.wireOp",EDGE,"E95");var subQ5=sQuery(id+"F0.wireOp",EDGE,"E115.MirrorCS");var subQ6=makeQuery(id+"F0.imprint","INTERSECT",VERTEX,{"derivedFrom":[subQ1,subQ5]});Q22=makeQuery(id+"F0.imprint","IMPRINT",FACE,{"disambiguationData":[TD([[makeQuery(id+"F0.imprint","IMPRINT",EDGE,{"disambiguationData":[TD([[subQ6,-1.0]])],"derivedFrom":subQ1}),-1.0]])]});}
            var Q23;
            {var subQ0=sQuery(id+"F0.wireOp",EDGE,"E119");var subQ1=sQuery(id+"F0.wireOp",EDGE,"E94");var subQ2=makeQuery(id+"F0.imprint","INTERSECT",VERTEX,{"derivedFrom":[subQ1,subQ0]});Q23=makeQuery(id+"F0.imprint","IMPRINT",FACE,{"disambiguationData":[TD([[makeQuery(id+"F0.imprint","IMPRINT",EDGE,{"disambiguationData":[TD([[subQ2,-1.0]])],"derivedFrom":subQ1}),1.0]])]});}
            var Q24;
            {var subQ0=sQuery(id+"F0.wireOp",EDGE,"E121.2");var subQ1=sQuery(id+"F0.wireOp",EDGE,"E84");var subQ2=makeQuery(id+"F0.imprint","INTERSECT",VERTEX,{"disambiguationData":[OD(0.0)],"derivedFrom":[subQ1,subQ0]});Q24=makeQuery(id+"F0.imprint","IMPRINT",FACE,{"disambiguationData":[TD([[makeQuery(id+"F0.imprint","IMPRINT",EDGE,{"disambiguationData":[TD([[subQ2,-1.0]])],"derivedFrom":subQ1}),1.0]])]});}
            var Q25;
            {var subQ0=sQuery(id+"F0.wireOp",EDGE,"E121.0");var subQ1=sQuery(id+"F0.wireOp",EDGE,"E97");var subQ2=makeQuery(id+"F0.imprint","INTERSECT",VERTEX,{"disambiguationData":[OD(0.0)],"derivedFrom":[subQ1,subQ0]});Q25=makeQuery(id+"F0.imprint","IMPRINT",FACE,{"disambiguationData":[TD([[makeQuery(id+"F0.imprint","IMPRINT",EDGE,{"disambiguationData":[TD([[subQ2,-1.0]])],"derivedFrom":subQ1}),-1.0]])]});}
            var Q26;
            {var subQ0=sQuery(id+"F0.wireOp",EDGE,"E119");var subQ1=sQuery(id+"F0.wireOp",EDGE,"E95");var subQ2=makeQuery(id+"F0.imprint","INTERSECT",VERTEX,{"derivedFrom":[subQ1,subQ0]});Q26=makeQuery(id+"F0.imprint","IMPRINT",FACE,{"disambiguationData":[TD([[makeQuery(id+"F0.imprint","IMPRINT",EDGE,{"disambiguationData":[TD([[subQ2,-1.0]])],"derivedFrom":subQ1}),-1.0]])]});}
            var Q27;
            {var subQ0=sQuery(id+"F0.wireOp",EDGE,"E117");var subQ1=sQuery(id+"F0.wireOp",EDGE,"E87");var subQ2=makeQuery(id+"F0.imprint","INTERSECT",VERTEX,{"derivedFrom":[subQ1,subQ0]});Q27=makeQuery(id+"F0.imprint","IMPRINT",FACE,{"disambiguationData":[TD([[makeQuery(id+"F0.imprint","IMPRINT",EDGE,{"disambiguationData":[TD([[subQ2,-1.0]])],"derivedFrom":subQ1}),-1.0]])]});}
            var Q28;
            {var subQ0=sQuery(id+"F0.wireOp",EDGE,"E121.2");var subQ1=sQuery(id+"F0.wireOp",EDGE,"E85");var subQ2=makeQuery(id+"F0.imprint","INTERSECT",VERTEX,{"disambiguationData":[OD(1.0)],"derivedFrom":[subQ1,subQ0]});Q28=makeQuery(id+"F0.imprint","IMPRINT",FACE,{"disambiguationData":[TD([[makeQuery(id+"F0.imprint","IMPRINT",EDGE,{"disambiguationData":[TD([[subQ2,-1.0]])],"derivedFrom":subQ1}),-1.0]])]});}
            extrude(context, id + "F4", {"entities" : qUnion([Q0, Q1, Q2, Q3, Q4, Q5, Q6, Q7, Q8, Q9, Q10, Q11, Q12, Q13, Q14, Q15, Q16, Q17, Q18, Q19, Q20, Q21, Q22, Q23, Q24, Q25, Q26, Q27, Q28]), "operationType" : NewBodyOperationType.ADD, "depth" : 10 * mm});
        }
        {
            var Q0;
            {var subQ0=sQuery(id+"F0.wireOp",EDGE,"E112");var subQ1=sQuery(id+"F0.wireOp",EDGE,"E84");var subQ2=makeQuery(id+"F0.imprint","INTERSECT",VERTEX,{"derivedFrom":[subQ1,subQ0]});Q0=makeQuery(id+"F0.imprint","IMPRINT",FACE,{"disambiguationData":[TD([[makeQuery(id+"F0.imprint","IMPRINT",EDGE,{"disambiguationData":[TD([[subQ2,-1.0]])],"derivedFrom":subQ1}),1.0]])]});}
            var Q1;
            {var subQ0=sQuery(id+"F0.wireOp",EDGE,"E84");var subQ1=makeQuery(id+"F0.imprint","INTERSECT",VERTEX,{"derivedFrom":[subQ0,sQuery(id+"F0.wireOp",EDGE,"E116.0")]});Q1=makeQuery(id+"F0.imprint","IMPRINT",FACE,{"disambiguationData":[TD([[makeQuery(id+"F0.imprint","IMPRINT",EDGE,{"disambiguationData":[TD([[subQ1,1.0]])],"derivedFrom":subQ0}),1.0]])]});}
            var Q2;
            {var subQ1=sQuery(id+"F0.wireOp",EDGE,"E85");var subQ5=sQuery(id+"F0.wireOp",EDGE,"E116.0");var subQ6=makeQuery(id+"F0.imprint","INTERSECT",VERTEX,{"derivedFrom":[subQ1,subQ5]});Q2=makeQuery(id+"F0.imprint","IMPRINT",FACE,{"disambiguationData":[TD([[makeQuery(id+"F0.imprint","IMPRINT",EDGE,{"disambiguationData":[TD([[subQ6,-1.0]])],"derivedFrom":subQ1}),-1.0]])]});}
            var Q3;
            {var subQ1=sQuery(id+"F0.wireOp",EDGE,"E85");var subQ5=sQuery(id+"F0.wireOp",EDGE,"E113");var subQ6=makeQuery(id+"F0.imprint","INTERSECT",VERTEX,{"derivedFrom":[subQ1,subQ5]});Q3=makeQuery(id+"F0.imprint","IMPRINT",FACE,{"disambiguationData":[TD([[makeQuery(id+"F0.imprint","IMPRINT",EDGE,{"disambiguationData":[TD([[subQ6,-1.0]])],"derivedFrom":subQ1}),-1.0]])]});}
            var Q4;
            {var subQ0=sQuery(id+"F0.wireOp",EDGE,"E114.0");var subQ1=sQuery(id+"F0.wireOp",EDGE,"E85");var subQ2=makeQuery(id+"F0.imprint","INTERSECT",VERTEX,{"derivedFrom":[subQ1,subQ0]});Q4=makeQuery(id+"F0.imprint","IMPRINT",FACE,{"disambiguationData":[TD([[makeQuery(id+"F0.imprint","IMPRINT",EDGE,{"disambiguationData":[TD([[subQ2,-1.0]])],"derivedFrom":subQ1}),-1.0]])]});}
            var Q5;
            {var subQ0=sQuery(id+"F0.wireOp",EDGE,"E112");var subQ1=sQuery(id+"F0.wireOp",EDGE,"E85");var subQ2=makeQuery(id+"F0.imprint","INTERSECT",VERTEX,{"derivedFrom":[subQ1,subQ0]});Q5=makeQuery(id+"F0.imprint","IMPRINT",FACE,{"disambiguationData":[TD([[makeQuery(id+"F0.imprint","IMPRINT",EDGE,{"disambiguationData":[TD([[subQ2,-1.0]])],"derivedFrom":subQ1}),-1.0]])]});}
            var Q6;
            {var subQ3=sQuery(id+"F0.wireOp",EDGE,"E112");var subQ5=sQuery(id+"F0.wireOp",EDGE,"E87");var subQ6=makeQuery(id+"F0.imprint","INTERSECT",VERTEX,{"derivedFrom":[subQ5,subQ3]});Q6=makeQuery(id+"F0.imprint","IMPRINT",FACE,{"disambiguationData":[TD([[makeQuery(id+"F0.imprint","IMPRINT",EDGE,{"disambiguationData":[TD([[subQ6,-1.0]])],"derivedFrom":subQ5}),-1.0]])]});}
            var Q7;
            {var subQ0=sQuery(id+"F0.wireOp",EDGE,"E114.0");var subQ1=sQuery(id+"F0.wireOp",EDGE,"E87");var subQ2=makeQuery(id+"F0.imprint","INTERSECT",VERTEX,{"derivedFrom":[subQ1,subQ0]});Q7=makeQuery(id+"F0.imprint","IMPRINT",FACE,{"disambiguationData":[TD([[makeQuery(id+"F0.imprint","IMPRINT",EDGE,{"disambiguationData":[TD([[subQ2,-1.0]])],"derivedFrom":subQ1}),-1.0]])]});}
            var Q8;
            {var subQ0=sQuery(id+"F0.wireOp",EDGE,"E136");var subQ1=sQuery(id+"F0.wireOp",EDGE,"E87");var subQ2=makeQuery(id+"F0.imprint","INTERSECT",VERTEX,{"disambiguationData":[OD(1.0)],"derivedFrom":[subQ1,subQ0]});Q8=makeQuery(id+"F0.imprint","IMPRINT",FACE,{"disambiguationData":[TD([[makeQuery(id+"F0.imprint","IMPRINT",EDGE,{"disambiguationData":[TD([[subQ2,-1.0]])],"derivedFrom":subQ1}),-1.0]])]});}
            var Q9;
            {var subQ0=sQuery(id+"F0.wireOp",EDGE,"E116.0");var subQ1=sQuery(id+"F0.wireOp",EDGE,"E87");var subQ2=makeQuery(id+"F0.imprint","INTERSECT",VERTEX,{"derivedFrom":[subQ1,subQ0]});Q9=makeQuery(id+"F0.imprint","IMPRINT",FACE,{"disambiguationData":[TD([[makeQuery(id+"F0.imprint","IMPRINT",EDGE,{"disambiguationData":[TD([[subQ2,-1.0]])],"derivedFrom":subQ1}),-1.0]])]});}
            var Q10;
            {var subQ0=sQuery(id+"F0.wireOp",EDGE,"E116.0");var subQ1=sQuery(id+"F0.wireOp",EDGE,"E89");var subQ2=makeQuery(id+"F0.imprint","INTERSECT",VERTEX,{"derivedFrom":[subQ1,subQ0]});Q10=makeQuery(id+"F0.imprint","IMPRINT",FACE,{"disambiguationData":[TD([[makeQuery(id+"F0.imprint","IMPRINT",EDGE,{"disambiguationData":[TD([[subQ2,-1.0]])],"derivedFrom":subQ1}),-1.0]])]});}
            var Q11;
            {var subQ0=sQuery(id+"F0.wireOp",EDGE,"E136");var subQ1=sQuery(id+"F0.wireOp",EDGE,"E89");var subQ2=makeQuery(id+"F0.imprint","INTERSECT",VERTEX,{"disambiguationData":[OD(1.0)],"derivedFrom":[subQ1,subQ0]});Q11=makeQuery(id+"F0.imprint","IMPRINT",FACE,{"disambiguationData":[TD([[makeQuery(id+"F0.imprint","IMPRINT",EDGE,{"disambiguationData":[TD([[subQ2,-1.0]])],"derivedFrom":subQ1}),-1.0]])]});}
            var Q12;
            {var subQ0=sQuery(id+"F0.wireOp",EDGE,"E114.0");var subQ1=sQuery(id+"F0.wireOp",EDGE,"E89");var subQ2=makeQuery(id+"F0.imprint","INTERSECT",VERTEX,{"derivedFrom":[subQ1,subQ0]});Q12=makeQuery(id+"F0.imprint","IMPRINT",FACE,{"disambiguationData":[TD([[makeQuery(id+"F0.imprint","IMPRINT",EDGE,{"disambiguationData":[TD([[subQ2,-1.0]])],"derivedFrom":subQ1}),-1.0]])]});}
            var Q13;
            {var subQ0=sQuery(id+"F0.wireOp",EDGE,"E106.MirrorCS");var subQ1=sQuery(id+"F0.wireOp",EDGE,"E89");var subQ2=makeQuery(id+"F0.imprint","INTERSECT",VERTEX,{"derivedFrom":[subQ1,subQ0]});Q13=makeQuery(id+"F0.imprint","IMPRINT",FACE,{"disambiguationData":[TD([[makeQuery(id+"F0.imprint","IMPRINT",EDGE,{"disambiguationData":[TD([[subQ2,-1.0]])],"derivedFrom":subQ1}),-1.0]])]});}
            var Q14;
            {var subQ0=sQuery(id+"F0.wireOp",EDGE,"E106.MirrorCS");var subQ1=sQuery(id+"F0.wireOp",EDGE,"E91");var subQ2=makeQuery(id+"F0.imprint","INTERSECT",VERTEX,{"derivedFrom":[subQ1,subQ0]});Q14=makeQuery(id+"F0.imprint","IMPRINT",FACE,{"disambiguationData":[TD([[makeQuery(id+"F0.imprint","IMPRINT",EDGE,{"disambiguationData":[TD([[subQ2,-1.0]])],"derivedFrom":subQ1}),-1.0]])]});}
            var Q15;
            {var subQ0=sQuery(id+"F0.wireOp",EDGE,"E114.0");var subQ1=sQuery(id+"F0.wireOp",EDGE,"E91");var subQ2=makeQuery(id+"F0.imprint","INTERSECT",VERTEX,{"derivedFrom":[subQ1,subQ0]});Q15=makeQuery(id+"F0.imprint","IMPRINT",FACE,{"disambiguationData":[TD([[makeQuery(id+"F0.imprint","IMPRINT",EDGE,{"disambiguationData":[TD([[subQ2,-1.0]])],"derivedFrom":subQ1}),-1.0]])]});}
            var Q16;
            {var subQ0=sQuery(id+"F0.wireOp",EDGE,"E136");var subQ1=sQuery(id+"F0.wireOp",EDGE,"E91");var subQ2=makeQuery(id+"F0.imprint","INTERSECT",VERTEX,{"disambiguationData":[OD(1.0)],"derivedFrom":[subQ1,subQ0]});Q16=makeQuery(id+"F0.imprint","IMPRINT",FACE,{"disambiguationData":[TD([[makeQuery(id+"F0.imprint","IMPRINT",EDGE,{"disambiguationData":[TD([[subQ2,-1.0]])],"derivedFrom":subQ1}),-1.0]])]});}
            var Q17;
            {var subQ0=sQuery(id+"F0.wireOp",EDGE,"E116.0");var subQ1=sQuery(id+"F0.wireOp",EDGE,"E91");var subQ2=makeQuery(id+"F0.imprint","INTERSECT",VERTEX,{"derivedFrom":[subQ1,subQ0]});Q17=makeQuery(id+"F0.imprint","IMPRINT",FACE,{"disambiguationData":[TD([[makeQuery(id+"F0.imprint","IMPRINT",EDGE,{"disambiguationData":[TD([[subQ2,-1.0]])],"derivedFrom":subQ1}),-1.0]])]});}
            var Q18;
            {var subQ1=sQuery(id+"F0.wireOp",EDGE,"E93");var subQ5=sQuery(id+"F0.wireOp",EDGE,"E116.0");var subQ12=makeQuery(id+"F0.imprint","INTERSECT",VERTEX,{"derivedFrom":[subQ1,subQ5]});Q18=makeQuery(id+"F0.imprint","IMPRINT",FACE,{"disambiguationData":[TD([[makeQuery(id+"F0.imprint","IMPRINT",EDGE,{"disambiguationData":[TD([[subQ12,-1.0]])],"derivedFrom":subQ1}),-1.0]])]});}
            var Q19;
            {var subQ0=sQuery(id+"F0.wireOp",EDGE,"E119");var subQ1=sQuery(id+"F0.wireOp",EDGE,"E94");var subQ2=makeQuery(id+"F0.imprint","INTERSECT",VERTEX,{"derivedFrom":[subQ1,subQ0]});Q19=makeQuery(id+"F0.imprint","IMPRINT",FACE,{"disambiguationData":[TD([[makeQuery(id+"F0.imprint","IMPRINT",EDGE,{"disambiguationData":[TD([[subQ2,-1.0]])],"derivedFrom":subQ1}),1.0]])]});}
            var Q20;
            {var subQ0=sQuery(id+"F0.wireOp",EDGE,"E136");var subQ1=sQuery(id+"F0.wireOp",EDGE,"E93");var subQ2=makeQuery(id+"F0.imprint","INTERSECT",VERTEX,{"disambiguationData":[OD(1.0)],"derivedFrom":[subQ1,subQ0]});Q20=makeQuery(id+"F0.imprint","IMPRINT",FACE,{"disambiguationData":[TD([[makeQuery(id+"F0.imprint","IMPRINT",EDGE,{"disambiguationData":[TD([[subQ2,-1.0]])],"derivedFrom":subQ1}),-1.0]])]});}
            var Q21;
            {var subQ0=sQuery(id+"F0.wireOp",EDGE,"E114.0");var subQ1=sQuery(id+"F0.wireOp",EDGE,"E93");var subQ2=makeQuery(id+"F0.imprint","INTERSECT",VERTEX,{"derivedFrom":[subQ1,subQ0]});Q21=makeQuery(id+"F0.imprint","IMPRINT",FACE,{"disambiguationData":[TD([[makeQuery(id+"F0.imprint","IMPRINT",EDGE,{"disambiguationData":[TD([[subQ2,-1.0]])],"derivedFrom":subQ1}),-1.0]])]});}
            var Q22;
            {var subQ3=sQuery(id+"F0.wireOp",EDGE,"E106.MirrorCS");var subQ7=sQuery(id+"F0.wireOp",EDGE,"E93");var subQ8=makeQuery(id+"F0.imprint","INTERSECT",VERTEX,{"derivedFrom":[subQ7,subQ3]});Q22=makeQuery(id+"F0.imprint","IMPRINT",FACE,{"disambiguationData":[TD([[makeQuery(id+"F0.imprint","IMPRINT",EDGE,{"disambiguationData":[TD([[subQ8,-1.0]])],"derivedFrom":subQ7}),-1.0]])]});}
            var Q23;
            {var subQ0=sQuery(id+"F0.wireOp",EDGE,"E112");var subQ1=sQuery(id+"F0.wireOp",EDGE,"E95");var subQ2=makeQuery(id+"F0.imprint","INTERSECT",VERTEX,{"derivedFrom":[subQ1,subQ0]});Q23=makeQuery(id+"F0.imprint","IMPRINT",FACE,{"disambiguationData":[TD([[makeQuery(id+"F0.imprint","IMPRINT",EDGE,{"disambiguationData":[TD([[subQ2,-1.0]])],"derivedFrom":subQ1}),-1.0]])]});}
            var Q24;
            {var subQ0=sQuery(id+"F0.wireOp",EDGE,"E114.0");var subQ1=sQuery(id+"F0.wireOp",EDGE,"E95");var subQ2=makeQuery(id+"F0.imprint","INTERSECT",VERTEX,{"derivedFrom":[subQ1,subQ0]});Q24=makeQuery(id+"F0.imprint","IMPRINT",FACE,{"disambiguationData":[TD([[makeQuery(id+"F0.imprint","IMPRINT",EDGE,{"disambiguationData":[TD([[subQ2,-1.0]])],"derivedFrom":subQ1}),-1.0]])]});}
            var Q25;
            {var subQ3=sQuery(id+"F0.wireOp",EDGE,"E136");var subQ6=sQuery(id+"F0.wireOp",EDGE,"E95");var subQ9=makeQuery(id+"F0.imprint","INTERSECT",VERTEX,{"disambiguationData":[OD(1.0)],"derivedFrom":[subQ6,subQ3]});Q25=makeQuery(id+"F0.imprint","IMPRINT",FACE,{"disambiguationData":[TD([[makeQuery(id+"F0.imprint","IMPRINT",EDGE,{"disambiguationData":[TD([[subQ9,-1.0]])],"derivedFrom":subQ6}),-1.0]])]});}
            var Q26;
            {var subQ5=sQuery(id+"F0.wireOp",EDGE,"E116.0");var subQ7=sQuery(id+"F0.wireOp",EDGE,"E95");var subQ8=makeQuery(id+"F0.imprint","INTERSECT",VERTEX,{"derivedFrom":[subQ7,subQ5]});Q26=makeQuery(id+"F0.imprint","IMPRINT",FACE,{"disambiguationData":[TD([[makeQuery(id+"F0.imprint","IMPRINT",EDGE,{"disambiguationData":[TD([[subQ8,-1.0]])],"derivedFrom":subQ7}),-1.0]])]});}
            var Q27;
            {var subQ0=sQuery(id+"F0.wireOp",EDGE,"E119");var subQ1=sQuery(id+"F0.wireOp",EDGE,"E95");var subQ2=makeQuery(id+"F0.imprint","INTERSECT",VERTEX,{"derivedFrom":[subQ1,subQ0]});Q27=makeQuery(id+"F0.imprint","IMPRINT",FACE,{"disambiguationData":[TD([[makeQuery(id+"F0.imprint","IMPRINT",EDGE,{"disambiguationData":[TD([[subQ2,-1.0]])],"derivedFrom":subQ1}),-1.0]])]});}
            var Q28;
            {var subQ0=sQuery(id+"F0.wireOp",EDGE,"E115.MirrorCS");var subQ3=sQuery(id+"F0.wireOp",EDGE,"E97");var subQ4=makeQuery(id+"F0.imprint","INTERSECT",VERTEX,{"derivedFrom":[subQ3,subQ0]});Q28=makeQuery(id+"F0.imprint","IMPRINT",FACE,{"disambiguationData":[TD([[makeQuery(id+"F0.imprint","IMPRINT",EDGE,{"disambiguationData":[TD([[subQ4,1.0]])],"derivedFrom":subQ3}),-1.0]])]});}
            var Q29;
            {var subQ0=sQuery(id+"F0.wireOp",EDGE,"E112");var subQ1=sQuery(id+"F0.wireOp",EDGE,"E97");var subQ2=makeQuery(id+"F0.imprint","INTERSECT",VERTEX,{"derivedFrom":[subQ1,subQ0]});Q29=makeQuery(id+"F0.imprint","IMPRINT",FACE,{"disambiguationData":[TD([[makeQuery(id+"F0.imprint","IMPRINT",EDGE,{"disambiguationData":[TD([[subQ2,-1.0]])],"derivedFrom":subQ1}),-1.0]])]});}
            var Q30;
            {var subQ0=sQuery(id+"F0.wireOp",EDGE,"E114.0");var subQ1=sQuery(id+"F0.wireOp",EDGE,"E97");var subQ2=makeQuery(id+"F0.imprint","INTERSECT",VERTEX,{"derivedFrom":[subQ1,subQ0]});Q30=makeQuery(id+"F0.imprint","IMPRINT",FACE,{"disambiguationData":[TD([[makeQuery(id+"F0.imprint","IMPRINT",EDGE,{"disambiguationData":[TD([[subQ2,-1.0]])],"derivedFrom":subQ1}),-1.0]])]});}
            var Q31;
            {var subQ0=sQuery(id+"F0.wireOp",EDGE,"E113");var subQ1=sQuery(id+"F0.wireOp",EDGE,"E97");var subQ2=makeQuery(id+"F0.imprint","INTERSECT",VERTEX,{"derivedFrom":[subQ1,subQ0]});Q31=makeQuery(id+"F0.imprint","IMPRINT",FACE,{"disambiguationData":[TD([[makeQuery(id+"F0.imprint","IMPRINT",EDGE,{"disambiguationData":[TD([[subQ2,-1.0]])],"derivedFrom":subQ1}),-1.0]])]});}
            extrude(context, id + "F5", {"entities" : qUnion([Q0, Q1, Q2, Q3, Q4, Q5, Q6, Q7, Q8, Q9, Q10, Q11, Q12, Q13, Q14, Q15, Q16, Q17, Q18, Q19, Q20, Q21, Q22, Q23, Q24, Q25, Q26, Q27, Q28, Q29, Q30, Q31]), "operationType" : NewBodyOperationType.ADD, "depth" : 10 * mm});
        }
        {
            var Q0;
            Q0=qCreatedBy(makeId("Top.planeOp"),FACE);
            var sketch = newSketch(context, id + "F6", { "sketchPlane" : qUnion([Q0])});
            skLineSegment(sketch, "E138.bottom", {"start": v(-49, -8.73) * mm, "end": v(52.88, -8.73) * mm});
            skLineSegment(sketch, "E138.top", {"start": v(-49, -35.48) * mm, "end": v(52.88, -35.48) * mm});
            skLineSegment(sketch, "E138.left", {"start": v(-49, -8.73) * mm, "end": v(-49, -35.48) * mm});
            skLineSegment(sketch, "E138.right", {"start": v(52.88, -8.73) * mm, "end": v(52.88, -35.48) * mm});
            skSolve(sketch);
        }
        {
            var Q0;
            Q0=makeQuery(id+"F6.imprint","IMPRINT",FACE,{"disambiguationData":[TD([[makeQuery(id+"F6.imprint","IMPRINT",EDGE,{"derivedFrom":sQuery(id+"F6.wireOp",EDGE,"E138.bottom")}),-1.0]])]});
            extrude(context, id + "F7", {"entities" : qUnion([Q0]), "depth" : 0.6 * mm});
        }
        {
            var Q0;
            Q0=makeQuery(id+"F7.opExtrude","SWEPT_EDGE",EDGE,{"disambiguationData":[OSD([sQuery(id+"F6.wireOp",EDGE,"E138.bottom"),sQuery(id+"F6.wireOp",EDGE,"E138.left")])]});
            var Q1;
            Q1=makeQuery(id+"F7.opExtrude","SWEPT_EDGE",EDGE,{"disambiguationData":[OSD([sQuery(id+"F6.wireOp",EDGE,"E138.top"),sQuery(id+"F6.wireOp",EDGE,"E138.left")])]});
            var Q2;
            Q2=makeQuery(id+"F7.opExtrude","SWEPT_EDGE",EDGE,{"disambiguationData":[OSD([sQuery(id+"F6.wireOp",EDGE,"E138.bottom"),sQuery(id+"F6.wireOp",EDGE,"E138.right")])]});
            var Q3;
            Q3=makeQuery(id+"F7.opExtrude","SWEPT_EDGE",EDGE,{"disambiguationData":[OSD([sQuery(id+"F6.wireOp",EDGE,"E138.top"),sQuery(id+"F6.wireOp",EDGE,"E138.right")])]});
            fillet(context, id + "F8", {"entities" : qUnion([Q0, Q1, Q2, Q3]), "radius" : 5 * mm, "tangentPropagation" : true, "allowEdgeOverflow" : false});
        }
        {
            var Q0;
            {var subQ0=sQuery(id+"F0.wireOp",EDGE,"E7");var subQ1=sQuery(id+"F0.wireOp",EDGE,"E6");var subQ2=sQuery(id+"F0.wireOp",EDGE,"E5");Q0=makeQuery(id+"F2.boolean.opBoolean","MERGE",FACE,{"derivedFrom":[makeQuery(id+"F1.opExtrude","CAP_FACE",FACE,{"disambiguationData":[OSD([sQuery(id+"F0.wireOp",EDGE,"E3"),sQuery(id+"F0.wireOp",EDGE,"E4"),subQ2,subQ1,subQ0,sQuery(id+"F0.wireOp",EDGE,"E122")])],"isStart":false}),makeQuery(id+"F2.opExtrude","CAP_FACE",FACE,{"disambiguationData":[OSD([subQ2,subQ1,subQ0,sQuery(id+"F0.wireOp",EDGE,"E54.MirrorCS"),sQuery(id+"F0.wireOp",EDGE,"E56.MirrorCS"),sQuery(id+"F0.wireOp",EDGE,"E84")])],"isStart":false})]});}
            var Q1;
            Q1=makeQuery(id+"F2.opExtrude","CAP_FACE",FACE,{"disambiguationData":[OSD([sQuery(id+"F0.wireOp",EDGE,"E3"),sQuery(id+"F0.wireOp",EDGE,"E56.MirrorCS"),sQuery(id+"F0.wireOp",EDGE,"E85"),sQuery(id+"F0.wireOp",EDGE,"E86"),sQuery(id+"F0.wireOp",EDGE,"E123"),sQuery(id+"F0.wireOp",EDGE,"E124")])],"isStart":false});
            var Q2;
            Q2=makeQuery(id+"F2.opExtrude","CAP_FACE",FACE,{"disambiguationData":[OSD([sQuery(id+"F0.wireOp",EDGE,"E3"),sQuery(id+"F0.wireOp",EDGE,"E56.MirrorCS"),sQuery(id+"F0.wireOp",EDGE,"E87"),sQuery(id+"F0.wireOp",EDGE,"E88"),sQuery(id+"F0.wireOp",EDGE,"E125"),sQuery(id+"F0.wireOp",EDGE,"E126")])],"isStart":false});
            var Q3;
            Q3=makeQuery(id+"F2.opExtrude","CAP_FACE",FACE,{"disambiguationData":[OSD([sQuery(id+"F0.wireOp",EDGE,"E3"),sQuery(id+"F0.wireOp",EDGE,"E33"),sQuery(id+"F0.wireOp",EDGE,"E56.MirrorCS"),sQuery(id+"F0.wireOp",EDGE,"E66.MirrorCS"),sQuery(id+"F0.wireOp",EDGE,"E89"),sQuery(id+"F0.wireOp",EDGE,"E90"),sQuery(id+"F0.wireOp",EDGE,"E127"),sQuery(id+"F0.wireOp",EDGE,"E128")])],"isStart":false});
            var Q4;
            Q4=makeQuery(id+"F2.opExtrude","CAP_FACE",FACE,{"disambiguationData":[OSD([sQuery(id+"F0.wireOp",EDGE,"E3"),sQuery(id+"F0.wireOp",EDGE,"E33"),sQuery(id+"F0.wireOp",EDGE,"E91"),sQuery(id+"F0.wireOp",EDGE,"E92"),sQuery(id+"F0.wireOp",EDGE,"E129"),sQuery(id+"F0.wireOp",EDGE,"E130")])],"isStart":false});
            var Q5;
            Q5=makeQuery(id+"F2.opExtrude","CAP_FACE",FACE,{"disambiguationData":[OSD([sQuery(id+"F0.wireOp",EDGE,"E3"),sQuery(id+"F0.wireOp",EDGE,"E33"),sQuery(id+"F0.wireOp",EDGE,"E34"),sQuery(id+"F0.wireOp",EDGE,"E56.MirrorCS"),sQuery(id+"F0.wireOp",EDGE,"E61.MirrorCS"),sQuery(id+"F0.wireOp",EDGE,"E66.MirrorCS"),sQuery(id+"F0.wireOp",EDGE,"E93"),sQuery(id+"F0.wireOp",EDGE,"E94"),sQuery(id+"F0.wireOp",EDGE,"E131"),sQuery(id+"F0.wireOp",EDGE,"E132")])],"isStart":false});
            var Q6;
            Q6=makeQuery(id+"F2.opExtrude","CAP_FACE",FACE,{"disambiguationData":[OSD([sQuery(id+"F0.wireOp",EDGE,"E3"),sQuery(id+"F0.wireOp",EDGE,"E56.MirrorCS"),sQuery(id+"F0.wireOp",EDGE,"E95"),sQuery(id+"F0.wireOp",EDGE,"E96"),sQuery(id+"F0.wireOp",EDGE,"E133"),sQuery(id+"F0.wireOp",EDGE,"E134")])],"isStart":false});
            var Q7;
            Q7=makeQuery(id+"F2.opExtrude","CAP_FACE",FACE,{"disambiguationData":[OSD([sQuery(id+"F0.wireOp",EDGE,"E56.MirrorCS"),sQuery(id+"F0.wireOp",EDGE,"E66.MirrorCS"),sQuery(id+"F0.wireOp",EDGE,"E91"),sQuery(id+"F0.wireOp",EDGE,"E92")])],"isStart":false});
            var Q8;
            Q8=makeQuery(id+"F3.opExtrude","CAP_FACE",FACE,{"disambiguationData":[OSD([sQuery(id+"F0.wireOp",EDGE,"E70"),sQuery(id+"F0.wireOp",EDGE,"E71"),sQuery(id+"F0.wireOp",EDGE,"E72"),sQuery(id+"F0.wireOp",EDGE,"E84")])],"isStart":false});
            var Q9;
            Q9=makeQuery(id+"F3.opExtrude","CAP_FACE",FACE,{"disambiguationData":[OSD([sQuery(id+"F0.wireOp",EDGE,"E70"),sQuery(id+"F0.wireOp",EDGE,"E72"),sQuery(id+"F0.wireOp",EDGE,"E85"),sQuery(id+"F0.wireOp",EDGE,"E86"),sQuery(id+"F0.wireOp",EDGE,"E103.MirrorCS"),sQuery(id+"F0.wireOp",EDGE,"E106.MirrorCS")])],"isStart":false});
            var Q10;
            Q10=makeQuery(id+"F3.opExtrude","CAP_FACE",FACE,{"disambiguationData":[OSD([sQuery(id+"F0.wireOp",EDGE,"E70"),sQuery(id+"F0.wireOp",EDGE,"E87"),sQuery(id+"F0.wireOp",EDGE,"E88"),sQuery(id+"F0.wireOp",EDGE,"E106.MirrorCS"),sQuery(id+"F0.wireOp",EDGE,"E112")])],"isStart":false});
            var Q11;
            Q11=makeQuery(id+"F3.opExtrude","CAP_FACE",FACE,{"disambiguationData":[OSD([sQuery(id+"F0.wireOp",EDGE,"E70"),sQuery(id+"F0.wireOp",EDGE,"E89"),sQuery(id+"F0.wireOp",EDGE,"E90"),sQuery(id+"F0.wireOp",EDGE,"E106.MirrorCS")])],"isStart":false});
            var Q12;
            Q12=makeQuery(id+"F3.opExtrude","CAP_FACE",FACE,{"disambiguationData":[OSD([sQuery(id+"F0.wireOp",EDGE,"E70"),sQuery(id+"F0.wireOp",EDGE,"E74"),sQuery(id+"F0.wireOp",EDGE,"E75"),sQuery(id+"F0.wireOp",EDGE,"E91"),sQuery(id+"F0.wireOp",EDGE,"E92"),sQuery(id+"F0.wireOp",EDGE,"E100.MirrorCS"),sQuery(id+"F0.wireOp",EDGE,"E102.MirrorCS"),sQuery(id+"F0.wireOp",EDGE,"E106.MirrorCS")])],"isStart":false});
            var Q13;
            Q13=makeQuery(id+"F3.opExtrude","CAP_FACE",FACE,{"disambiguationData":[OSD([sQuery(id+"F0.wireOp",EDGE,"E93"),sQuery(id+"F0.wireOp",EDGE,"E94"),sQuery(id+"F0.wireOp",EDGE,"E100.MirrorCS"),sQuery(id+"F0.wireOp",EDGE,"E106.MirrorCS")])],"isStart":false});
            var Q14;
            Q14=makeQuery(id+"F3.opExtrude","CAP_FACE",FACE,{"disambiguationData":[OSD([sQuery(id+"F0.wireOp",EDGE,"E95"),sQuery(id+"F0.wireOp",EDGE,"E96"),sQuery(id+"F0.wireOp",EDGE,"E100.MirrorCS"),sQuery(id+"F0.wireOp",EDGE,"E106.MirrorCS")])],"isStart":false});
            var Q15;
            Q15=makeQuery(id+"F3.opExtrude","CAP_FACE",FACE,{"disambiguationData":[OSD([sQuery(id+"F0.wireOp",EDGE,"E97"),sQuery(id+"F0.wireOp",EDGE,"E100.MirrorCS"),sQuery(id+"F0.wireOp",EDGE,"E106.MirrorCS"),sQuery(id+"F0.wireOp",EDGE,"E108.MirrorCS")])],"isStart":false});
            var Q16;
            Q16=makeQuery(id+"F3.opExtrude","CAP_FACE",FACE,{"disambiguationData":[OSD([sQuery(id+"F0.wireOp",EDGE,"E73"),sQuery(id+"F0.wireOp",EDGE,"E74"),sQuery(id+"F0.wireOp",EDGE,"E95"),sQuery(id+"F0.wireOp",EDGE,"E98.MirrorCS"),sQuery(id+"F0.wireOp",EDGE,"E102.MirrorCS")])],"isStart":false});
            var Q17;
            Q17=makeQuery(id+"F3.opExtrude","CAP_FACE",FACE,{"disambiguationData":[OSD([sQuery(id+"F0.wireOp",EDGE,"E74"),sQuery(id+"F0.wireOp",EDGE,"E93"),sQuery(id+"F0.wireOp",EDGE,"E94"),sQuery(id+"F0.wireOp",EDGE,"E102.MirrorCS")])],"isStart":false});
            var Q18;
            Q18=makeQuery(id+"F3.opExtrude","CAP_FACE",FACE,{"disambiguationData":[OSD([sQuery(id+"F0.wireOp",EDGE,"E70"),sQuery(id+"F0.wireOp",EDGE,"E75"),sQuery(id+"F0.wireOp",EDGE,"E93"),sQuery(id+"F0.wireOp",EDGE,"E94")])],"isStart":false});
            var Q19;
            Q19=makeQuery(id+"F3.opExtrude","CAP_FACE",FACE,{"disambiguationData":[OSD([sQuery(id+"F0.wireOp",EDGE,"E70"),sQuery(id+"F0.wireOp",EDGE,"E75"),sQuery(id+"F0.wireOp",EDGE,"E95"),sQuery(id+"F0.wireOp",EDGE,"E96")])],"isStart":false});
            var Q20;
            Q20=makeQuery(id+"F3.opExtrude","CAP_FACE",FACE,{"disambiguationData":[OSD([sQuery(id+"F0.wireOp",EDGE,"E73"),sQuery(id+"F0.wireOp",EDGE,"E74"),sQuery(id+"F0.wireOp",EDGE,"E95"),sQuery(id+"F0.wireOp",EDGE,"E98.MirrorCS"),sQuery(id+"F0.wireOp",EDGE,"E102.MirrorCS")])],"isStart":false});
            var Q21;
            Q21=makeQuery(id+"F3.opExtrude","CAP_FACE",FACE,{"disambiguationData":[OSD([sQuery(id+"F0.wireOp",EDGE,"E84"),sQuery(id+"F0.wireOp",EDGE,"E103.MirrorCS"),sQuery(id+"F0.wireOp",EDGE,"E104.MirrorCS"),sQuery(id+"F0.wireOp",EDGE,"E106.MirrorCS")])],"isStart":false});
            var Q22;
            {var subQ0=sQuery(id+"F0.wireOp",EDGE,"E97");var subQ1=sQuery(id+"F0.wireOp",EDGE,"E69");Q22=makeQuery(id+"F3.boolean.opBoolean","MERGE",FACE,{"derivedFrom":[makeQuery(id+"F2.opExtrude","CAP_FACE",FACE,{"disambiguationData":[OSD([sQuery(id+"F0.wireOp",EDGE,"E0"),sQuery(id+"F0.wireOp",EDGE,"E1"),sQuery(id+"F0.wireOp",EDGE,"E2"),sQuery(id+"F0.wireOp",EDGE,"E3"),sQuery(id+"F0.wireOp",EDGE,"E56.MirrorCS"),sQuery(id+"F0.wireOp",EDGE,"E57.MirrorCS"),sQuery(id+"F0.wireOp",EDGE,"E59.MirrorCS"),sQuery(id+"F0.wireOp",EDGE,"E62.MirrorCS"),subQ1,subQ0,sQuery(id+"F0.wireOp",EDGE,"E135")])],"isStart":false}),makeQuery(id+"F3.opExtrude","CAP_FACE",FACE,{"disambiguationData":[OSD([subQ1,sQuery(id+"F0.wireOp",EDGE,"E70"),sQuery(id+"F0.wireOp",EDGE,"E75"),subQ0])],"isStart":false})]});}
            chamfer(context, id + "F9", {"entities" : qUnion([Q0, Q1, Q2, Q3, Q4, Q5, Q6, Q7, Q8, Q9, Q10, Q11, Q12, Q13, Q14, Q15, Q16, Q17, Q18, Q19, Q20, Q21, Q22]), "width" : 0.3 * mm, "tangentPropagation" : true});
        }
        {
            var Q0;
            Q0=makeQuery(id+"F5.opExtrude","CAP_FACE",FACE,{"disambiguationData":[OSD([sQuery(id+"F0.wireOp",EDGE,"E84"),sQuery(id+"F0.wireOp",EDGE,"E112"),sQuery(id+"F0.wireOp",EDGE,"E115.MirrorCS")])],"isStart":false});
            var Q1;
            Q1=makeQuery(id+"F5.opExtrude","CAP_FACE",FACE,{"disambiguationData":[OSD([sQuery(id+"F0.wireOp",EDGE,"E85"),sQuery(id+"F0.wireOp",EDGE,"E86"),sQuery(id+"F0.wireOp",EDGE,"E112"),sQuery(id+"F0.wireOp",EDGE,"E115.MirrorCS"),sQuery(id+"F0.wireOp",EDGE,"E117"),sQuery(id+"F0.wireOp",EDGE,"E136")])],"isStart":false});
            var Q2;
            Q2=makeQuery(id+"F5.opExtrude","CAP_FACE",FACE,{"disambiguationData":[OSD([sQuery(id+"F0.wireOp",EDGE,"E87"),sQuery(id+"F0.wireOp",EDGE,"E88"),sQuery(id+"F0.wireOp",EDGE,"E106.MirrorCS"),sQuery(id+"F0.wireOp",EDGE,"E112"),sQuery(id+"F0.wireOp",EDGE,"E136")])],"isStart":false});
            var Q3;
            Q3=makeQuery(id+"F5.opExtrude","CAP_FACE",FACE,{"disambiguationData":[OSD([sQuery(id+"F0.wireOp",EDGE,"E89"),sQuery(id+"F0.wireOp",EDGE,"E90"),sQuery(id+"F0.wireOp",EDGE,"E106.MirrorCS"),sQuery(id+"F0.wireOp",EDGE,"E136")])],"isStart":false});
            var Q4;
            Q4=makeQuery(id+"F5.opExtrude","CAP_FACE",FACE,{"disambiguationData":[OSD([sQuery(id+"F0.wireOp",EDGE,"E89"),sQuery(id+"F0.wireOp",EDGE,"E90"),sQuery(id+"F0.wireOp",EDGE,"E115.MirrorCS"),sQuery(id+"F0.wireOp",EDGE,"E136")])],"isStart":false});
            var Q5;
            {var subQ0=sQuery(id+"F0.wireOp",EDGE,"E87");var subQ1=makeQuery(id+"F0.imprint","INTERSECT",VERTEX,{"derivedFrom":[subQ0,sQuery(id+"F0.wireOp",EDGE,"E116.0")]});Q5=makeQuery(id+"F5.opExtrude","CAP_EDGE",EDGE,{"disambiguationData":[OSD([subQ0]),TDD([makeQuery(id+"F0.imprint","IMPRINT",EDGE,{"disambiguationData":[TD([[makeQuery(id+"F0.imprint","INTERSECT",VERTEX,{"disambiguationData":[OD(1.0)],"derivedFrom":[subQ0,sQuery(id+"F0.wireOp",EDGE,"E136")]}),-1.0]])],"derivedFrom":subQ0}),makeQuery(id+"F0.imprint","IMPRINT",EDGE,{"disambiguationData":[TD([[subQ1,-1.0]])],"derivedFrom":subQ0})])],"isStart":false});}
            var Q6;
            Q6=makeQuery(id+"F5.opExtrude","CAP_FACE",FACE,{"disambiguationData":[OSD([sQuery(id+"F0.wireOp",EDGE,"E91"),sQuery(id+"F0.wireOp",EDGE,"E92"),sQuery(id+"F0.wireOp",EDGE,"E115.MirrorCS"),sQuery(id+"F0.wireOp",EDGE,"E136")])],"isStart":false});
            var Q7;
            Q7=makeQuery(id+"F5.opExtrude","CAP_FACE",FACE,{"disambiguationData":[OSD([sQuery(id+"F0.wireOp",EDGE,"E93"),sQuery(id+"F0.wireOp",EDGE,"E94"),sQuery(id+"F0.wireOp",EDGE,"E115.MirrorCS"),sQuery(id+"F0.wireOp",EDGE,"E136")])],"isStart":false});
            var Q8;
            Q8=makeQuery(id+"F5.opExtrude","CAP_FACE",FACE,{"disambiguationData":[OSD([sQuery(id+"F0.wireOp",EDGE,"E95"),sQuery(id+"F0.wireOp",EDGE,"E96"),sQuery(id+"F0.wireOp",EDGE,"E112"),sQuery(id+"F0.wireOp",EDGE,"E115.MirrorCS"),sQuery(id+"F0.wireOp",EDGE,"E136")])],"isStart":false});
            var Q9;
            Q9=makeQuery(id+"F5.opExtrude","CAP_FACE",FACE,{"disambiguationData":[OSD([sQuery(id+"F0.wireOp",EDGE,"E93"),sQuery(id+"F0.wireOp",EDGE,"E94"),sQuery(id+"F0.wireOp",EDGE,"E106.MirrorCS"),sQuery(id+"F0.wireOp",EDGE,"E112"),sQuery(id+"F0.wireOp",EDGE,"E136")])],"isStart":false});
            var Q10;
            Q10=makeQuery(id+"F5.opExtrude","CAP_FACE",FACE,{"disambiguationData":[OSD([sQuery(id+"F0.wireOp",EDGE,"E91"),sQuery(id+"F0.wireOp",EDGE,"E92"),sQuery(id+"F0.wireOp",EDGE,"E106.MirrorCS"),sQuery(id+"F0.wireOp",EDGE,"E136")])],"isStart":false});
            var Q11;
            Q11=makeQuery(id+"F5.opExtrude","CAP_FACE",FACE,{"disambiguationData":[OSD([sQuery(id+"F0.wireOp",EDGE,"E97"),sQuery(id+"F0.wireOp",EDGE,"E112"),sQuery(id+"F0.wireOp",EDGE,"E115.MirrorCS")])],"isStart":false});
            chamfer(context, id + "F10", {"entities" : qUnion([Q0, Q1, Q2, Q3, Q4, Q5, Q6, Q7, Q8, Q9, Q10, Q11]), "width" : 0.3 * mm, "tangentPropagation" : true});
        }
        {
            var Q0;
            Q0=makeQuery(id+"F4.opExtrude","CAP_FACE",FACE,{"disambiguationData":[OSD([sQuery(id+"F0.wireOp",EDGE,"E84"),sQuery(id+"F0.wireOp",EDGE,"E117"),sQuery(id+"F0.wireOp",EDGE,"E120")])],"isStart":false});
            var Q1;
            Q1=makeQuery(id+"F4.opExtrude","CAP_FACE",FACE,{"disambiguationData":[OSD([sQuery(id+"F0.wireOp",EDGE,"E85"),sQuery(id+"F0.wireOp",EDGE,"E86"),sQuery(id+"F0.wireOp",EDGE,"E115.MirrorCS"),sQuery(id+"F0.wireOp",EDGE,"E117"),sQuery(id+"F0.wireOp",EDGE,"E118")])],"isStart":false});
            var Q2;
            Q2=makeQuery(id+"F4.opExtrude","CAP_FACE",FACE,{"disambiguationData":[OSD([sQuery(id+"F0.wireOp",EDGE,"E87"),sQuery(id+"F0.wireOp",EDGE,"E88"),sQuery(id+"F0.wireOp",EDGE,"E117"),sQuery(id+"F0.wireOp",EDGE,"E118")])],"isStart":false});
            var Q3;
            Q3=makeQuery(id+"F4.opExtrude","CAP_FACE",FACE,{"disambiguationData":[OSD([sQuery(id+"F0.wireOp",EDGE,"E89"),sQuery(id+"F0.wireOp",EDGE,"E90"),sQuery(id+"F0.wireOp",EDGE,"E117"),sQuery(id+"F0.wireOp",EDGE,"E118")])],"isStart":false});
            var Q4;
            Q4=makeQuery(id+"F4.opExtrude","CAP_FACE",FACE,{"disambiguationData":[OSD([sQuery(id+"F0.wireOp",EDGE,"E91"),sQuery(id+"F0.wireOp",EDGE,"E92"),sQuery(id+"F0.wireOp",EDGE,"E117"),sQuery(id+"F0.wireOp",EDGE,"E118")])],"isStart":false});
            var Q5;
            Q5=makeQuery(id+"F4.opExtrude","CAP_FACE",FACE,{"disambiguationData":[OSD([sQuery(id+"F0.wireOp",EDGE,"E93"),sQuery(id+"F0.wireOp",EDGE,"E94"),sQuery(id+"F0.wireOp",EDGE,"E117"),sQuery(id+"F0.wireOp",EDGE,"E118")])],"isStart":false});
            var Q6;
            Q6=makeQuery(id+"F4.opExtrude","CAP_FACE",FACE,{"disambiguationData":[OSD([sQuery(id+"F0.wireOp",EDGE,"E95"),sQuery(id+"F0.wireOp",EDGE,"E96"),sQuery(id+"F0.wireOp",EDGE,"E117"),sQuery(id+"F0.wireOp",EDGE,"E118")])],"isStart":false});
            var Q7;
            Q7=makeQuery(id+"F4.opExtrude","CAP_FACE",FACE,{"disambiguationData":[OSD([sQuery(id+"F0.wireOp",EDGE,"E97"),sQuery(id+"F0.wireOp",EDGE,"E117"),sQuery(id+"F0.wireOp",EDGE,"E118"),sQuery(id+"F0.wireOp",EDGE,"E119")])],"isStart":false});
            var Q8;
            Q8=makeQuery(id+"F4.opExtrude","CAP_FACE",FACE,{"disambiguationData":[OSD([sQuery(id+"F0.wireOp",EDGE,"E95"),sQuery(id+"F0.wireOp",EDGE,"E96"),sQuery(id+"F0.wireOp",EDGE,"E117"),sQuery(id+"F0.wireOp",EDGE,"E119")])],"isStart":false});
            var Q9;
            Q9=makeQuery(id+"F4.opExtrude","CAP_FACE",FACE,{"disambiguationData":[OSD([sQuery(id+"F0.wireOp",EDGE,"E87"),sQuery(id+"F0.wireOp",EDGE,"E88"),sQuery(id+"F0.wireOp",EDGE,"E118"),sQuery(id+"F0.wireOp",EDGE,"E120")])],"isStart":false});
            var Q10;
            Q10=makeQuery(id+"F4.opExtrude","CAP_FACE",FACE,{"disambiguationData":[OSD([sQuery(id+"F0.wireOp",EDGE,"E85"),sQuery(id+"F0.wireOp",EDGE,"E86"),sQuery(id+"F0.wireOp",EDGE,"E118"),sQuery(id+"F0.wireOp",EDGE,"E120")])],"isStart":false});
            chamfer(context, id + "F11", {"entities" : qUnion([Q0, Q1, Q2, Q3, Q4, Q5, Q6, Q7, Q8, Q9, Q10]), "width" : 0.3 * mm, "tangentPropagation" : true});
        }
    });
